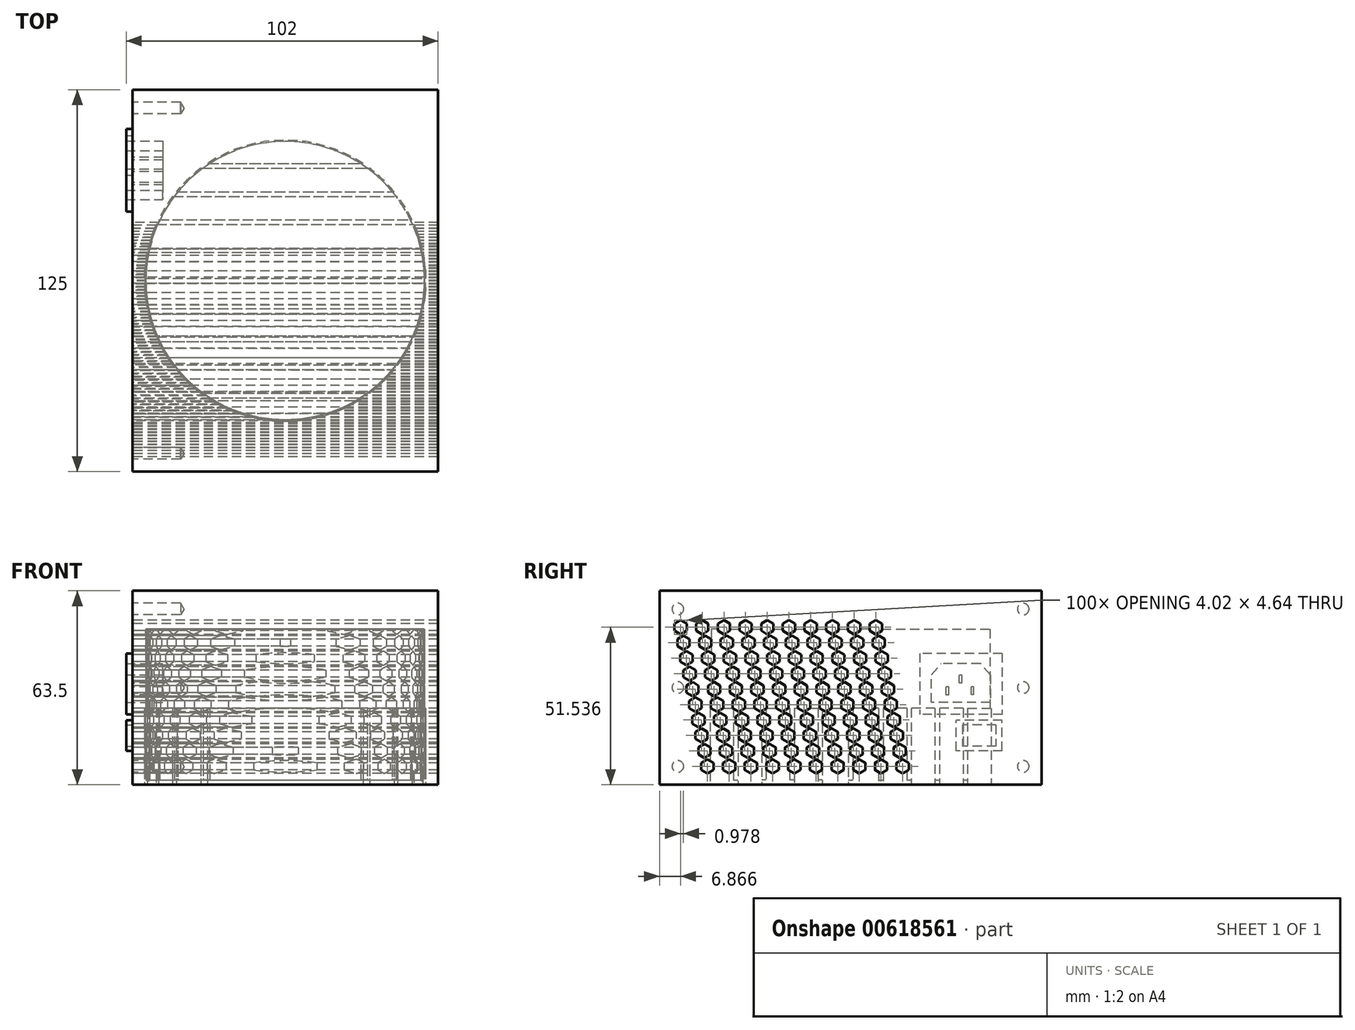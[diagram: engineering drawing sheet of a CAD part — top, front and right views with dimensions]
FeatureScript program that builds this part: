
annotation { "Feature Type Name" : "Feature", "Feature Type Description" : "" }
export const myFeature = defineFeature(function(context is Context, id is Id, definition is map)
    precondition{}
    {
        {
            var Q0;
            Q0=qCreatedBy(makeId("Top.planeOp"),FACE);
            var sketch = newSketch(context, id + "F0", { "sketchPlane" : qUnion([Q0])});
            skLineSegment(sketch, "E0.bottom", {"start": v(50, 62.5) * mm, "end": v(-50, 62.5) * mm});
            skLineSegment(sketch, "E0.top", {"start": v(50, -62.5) * mm, "end": v(-50, -62.5) * mm});
            skLineSegment(sketch, "E0.left", {"start": v(50, 62.5) * mm, "end": v(50, -62.5) * mm});
            skLineSegment(sketch, "E0.right", {"start": v(-50, 62.5) * mm, "end": v(-50, -62.5) * mm});
            skPoint(sketch, "E0.middle", {"position": v(0, 0) * mm});
            skSolve(sketch);
        }
        {
            var Q0;
            Q0=qSketchRegion(id+"F0",true);
            extrude(context, id + "F1", {"entities" : qUnion([Q0]), "depth" : 63.5 * mm, "offsetDistance" : 25 * mm});
        }
        {
            var Q0;
            Q0=makeQuery(id+"F1.opExtrude","SWEPT_FACE",FACE,{"disambiguationData":[OSD([sQuery(id+"F0.wireOp",EDGE,"E0.right")])]});
            var sketch = newSketch(context, id + "F2", { "sketchPlane" : qUnion([Q0])});
            skPoint(sketch, "E1", {"position": v(-56.5, 6) * mm});
            skPoint(sketch, "E2", {"position": v(-56.5, 57.5) * mm});
            skPoint(sketch, "E3", {"position": v(-56.5, 31.8) * mm});
            skPoint(sketch, "E4", {"position": v(56.5, 6) * mm});
            skPoint(sketch, "E5", {"position": v(56.5, 31.8) * mm});
            skPoint(sketch, "E6", {"position": v(56.5, 57.5) * mm});
            skLineSegment(sketch, "E7.bottom", {"start": v(-49.6, 42.98) * mm, "end": v(-22.6, 42.98) * mm});
            skLineSegment(sketch, "E7.top", {"start": v(-49.6, 22.98) * mm, "end": v(-22.6, 22.98) * mm});
            skLineSegment(sketch, "E7.left", {"start": v(-49.6, 42.98) * mm, "end": v(-49.6, 22.98) * mm});
            skLineSegment(sketch, "E7.right", {"start": v(-22.6, 42.98) * mm, "end": v(-22.6, 22.98) * mm});
            skLineSegment(sketch, "E8.bottom", {"start": v(-49.6, 11.07) * mm, "end": v(-34.6, 11.07) * mm});
            skLineSegment(sketch, "E8.top", {"start": v(-49.6, 21.07) * mm, "end": v(-34.6, 21.07) * mm});
            skLineSegment(sketch, "E8.left", {"start": v(-49.6, 11.07) * mm, "end": v(-49.6, 21.07) * mm});
            skLineSegment(sketch, "E8.right", {"start": v(-34.6, 11.07) * mm, "end": v(-34.6, 21.07) * mm});
            skLineSegment(sketch, "E9", {"start": v(-56.5, 6) * mm, "end": v(56.5, 6) * mm});
            skCircle(sketch, "E10.cCircle", {"center": v(-17.07, 6) * mm, "radius": 2 * mm, "construction": true});
            skLineSegment(sketch, "E10.0", {"start": v(-15.06, 7.16) * mm, "end": v(-15.06, 4.84) * mm});
            skLineSegment(sketch, "E10.1", {"start": v(-15.06, 4.84) * mm, "end": v(-17.07, 3.68) * mm});
            skLineSegment(sketch, "E10.2", {"start": v(-17.07, 3.68) * mm, "end": v(-19.08, 4.84) * mm});
            skLineSegment(sketch, "E10.3", {"start": v(-19.08, 4.84) * mm, "end": v(-19.08, 7.16) * mm});
            skLineSegment(sketch, "E10.4", {"start": v(-19.08, 7.16) * mm, "end": v(-17.07, 8.32) * mm});
            skLineSegment(sketch, "E10.5", {"start": v(-17.07, 8.32) * mm, "end": v(-15.06, 7.16) * mm});
            skPoint(sketch, "E10.0.midPoint", {"position": v(-15.06, 6) * mm});
            skLineSegment(sketch, "E11.0.1.0", {"start": v(-18.1, 12.22) * mm, "end": v(-16.1, 13.38) * mm});
            skLineSegment(sketch, "E11.0.1.1", {"start": v(-16.1, 13.38) * mm, "end": v(-14.08, 12.22) * mm});
            skLineSegment(sketch, "E11.0.1.2", {"start": v(-14.08, 12.22) * mm, "end": v(-14.08, 9.9) * mm});
            skLineSegment(sketch, "E11.0.1.3", {"start": v(-14.08, 9.9) * mm, "end": v(-16.1, 8.74) * mm});
            skLineSegment(sketch, "E11.0.1.4", {"start": v(-16.1, 8.74) * mm, "end": v(-18.1, 9.9) * mm});
            skLineSegment(sketch, "E11.0.1.5", {"start": v(-18.1, 9.9) * mm, "end": v(-18.1, 12.22) * mm});
            skLineSegment(sketch, "E11.0.2.0", {"start": v(-17.12, 17.28) * mm, "end": v(-15.11, 18.44) * mm});
            skLineSegment(sketch, "E11.0.2.1", {"start": v(-15.11, 18.44) * mm, "end": v(-13.1, 17.28) * mm});
            skLineSegment(sketch, "E11.0.2.2", {"start": v(-13.1, 17.28) * mm, "end": v(-13.1, 14.96) * mm});
            skLineSegment(sketch, "E11.0.2.3", {"start": v(-13.1, 14.96) * mm, "end": v(-15.11, 13.8) * mm});
            skLineSegment(sketch, "E11.0.2.4", {"start": v(-15.11, 13.8) * mm, "end": v(-17.12, 14.96) * mm});
            skLineSegment(sketch, "E11.0.2.5", {"start": v(-17.12, 14.96) * mm, "end": v(-17.12, 17.28) * mm});
            skLineSegment(sketch, "E11.0.3.0", {"start": v(-16.14, 22.34) * mm, "end": v(-14.14, 23.5) * mm});
            skLineSegment(sketch, "E11.0.3.1", {"start": v(-14.14, 23.5) * mm, "end": v(-12.13, 22.34) * mm});
            skLineSegment(sketch, "E11.0.3.2", {"start": v(-12.13, 22.34) * mm, "end": v(-12.13, 20.02) * mm});
            skLineSegment(sketch, "E11.0.3.3", {"start": v(-12.13, 20.02) * mm, "end": v(-14.14, 18.86) * mm});
            skLineSegment(sketch, "E11.0.3.4", {"start": v(-14.14, 18.86) * mm, "end": v(-16.14, 20.02) * mm});
            skLineSegment(sketch, "E11.0.3.5", {"start": v(-16.14, 20.02) * mm, "end": v(-16.14, 22.34) * mm});
            skLineSegment(sketch, "E11.0.4.0", {"start": v(-15.17, 27.4) * mm, "end": v(-13.16, 28.56) * mm});
            skLineSegment(sketch, "E11.0.4.1", {"start": v(-13.16, 28.56) * mm, "end": v(-11.15, 27.4) * mm});
            skLineSegment(sketch, "E11.0.4.2", {"start": v(-11.15, 27.4) * mm, "end": v(-11.15, 25.08) * mm});
            skLineSegment(sketch, "E11.0.4.3", {"start": v(-11.15, 25.08) * mm, "end": v(-13.16, 23.92) * mm});
            skLineSegment(sketch, "E11.0.4.4", {"start": v(-13.16, 23.92) * mm, "end": v(-15.17, 25.08) * mm});
            skLineSegment(sketch, "E11.0.4.5", {"start": v(-15.17, 25.08) * mm, "end": v(-15.17, 27.4) * mm});
            skLineSegment(sketch, "E11.0.5.0", {"start": v(-14.19, 32.46) * mm, "end": v(-12.18, 33.62) * mm});
            skLineSegment(sketch, "E11.0.5.1", {"start": v(-12.18, 33.62) * mm, "end": v(-10.17, 32.46) * mm});
            skLineSegment(sketch, "E11.0.5.2", {"start": v(-10.17, 32.46) * mm, "end": v(-10.17, 30.14) * mm});
            skLineSegment(sketch, "E11.0.5.3", {"start": v(-10.17, 30.14) * mm, "end": v(-12.18, 28.98) * mm});
            skLineSegment(sketch, "E11.0.5.4", {"start": v(-12.18, 28.98) * mm, "end": v(-14.19, 30.14) * mm});
            skLineSegment(sketch, "E11.0.5.5", {"start": v(-14.19, 30.14) * mm, "end": v(-14.19, 32.46) * mm});
            skLineSegment(sketch, "E11.0.6.0", {"start": v(-13.2, 37.52) * mm, "end": v(-11.2, 38.68) * mm});
            skLineSegment(sketch, "E11.0.6.1", {"start": v(-11.2, 38.68) * mm, "end": v(-9.2, 37.52) * mm});
            skLineSegment(sketch, "E11.0.6.2", {"start": v(-9.2, 37.52) * mm, "end": v(-9.2, 35.2) * mm});
            skLineSegment(sketch, "E11.0.6.3", {"start": v(-9.2, 35.2) * mm, "end": v(-11.2, 34.04) * mm});
            skLineSegment(sketch, "E11.0.6.4", {"start": v(-11.2, 34.04) * mm, "end": v(-13.2, 35.2) * mm});
            skLineSegment(sketch, "E11.0.6.5", {"start": v(-13.2, 35.2) * mm, "end": v(-13.2, 37.52) * mm});
            skLineSegment(sketch, "E11.0.7.0", {"start": v(-12.23, 42.58) * mm, "end": v(-10.22, 43.74) * mm});
            skLineSegment(sketch, "E11.0.7.1", {"start": v(-10.22, 43.74) * mm, "end": v(-8.21, 42.58) * mm});
            skLineSegment(sketch, "E11.0.7.2", {"start": v(-8.21, 42.58) * mm, "end": v(-8.21, 40.26) * mm});
            skLineSegment(sketch, "E11.0.7.3", {"start": v(-8.21, 40.26) * mm, "end": v(-10.22, 39.1) * mm});
            skLineSegment(sketch, "E11.0.7.4", {"start": v(-10.22, 39.1) * mm, "end": v(-12.23, 40.26) * mm});
            skLineSegment(sketch, "E11.0.7.5", {"start": v(-12.23, 40.26) * mm, "end": v(-12.23, 42.58) * mm});
            skLineSegment(sketch, "E11.0.8.0", {"start": v(-11.25, 47.64) * mm, "end": v(-9.24, 48.8) * mm});
            skLineSegment(sketch, "E11.0.8.1", {"start": v(-9.24, 48.8) * mm, "end": v(-7.24, 47.64) * mm});
            skLineSegment(sketch, "E11.0.8.2", {"start": v(-7.24, 47.64) * mm, "end": v(-7.24, 45.32) * mm});
            skLineSegment(sketch, "E11.0.8.3", {"start": v(-7.24, 45.32) * mm, "end": v(-9.24, 44.16) * mm});
            skLineSegment(sketch, "E11.0.8.4", {"start": v(-9.24, 44.16) * mm, "end": v(-11.25, 45.32) * mm});
            skLineSegment(sketch, "E11.0.8.5", {"start": v(-11.25, 45.32) * mm, "end": v(-11.25, 47.64) * mm});
            skLineSegment(sketch, "E11.0.9.0", {"start": v(-10.27, 52.7) * mm, "end": v(-8.27, 53.86) * mm});
            skLineSegment(sketch, "E11.0.9.1", {"start": v(-8.27, 53.86) * mm, "end": v(-6.26, 52.7) * mm});
            skLineSegment(sketch, "E11.0.9.2", {"start": v(-6.26, 52.7) * mm, "end": v(-6.26, 50.38) * mm});
            skLineSegment(sketch, "E11.0.9.3", {"start": v(-6.26, 50.38) * mm, "end": v(-8.27, 49.22) * mm});
            skLineSegment(sketch, "E11.0.9.4", {"start": v(-8.27, 49.22) * mm, "end": v(-10.27, 50.38) * mm});
            skLineSegment(sketch, "E11.0.9.5", {"start": v(-10.27, 50.38) * mm, "end": v(-10.27, 52.7) * mm});
            skLineSegment(sketch, "E11.1.0.0", {"start": v(-11.98, 7.16) * mm, "end": v(-9.97, 8.32) * mm});
            skLineSegment(sketch, "E11.1.0.1", {"start": v(-9.97, 8.32) * mm, "end": v(-7.96, 7.16) * mm});
            skLineSegment(sketch, "E11.1.0.2", {"start": v(-7.96, 7.16) * mm, "end": v(-7.96, 4.84) * mm});
            skLineSegment(sketch, "E11.1.0.3", {"start": v(-7.96, 4.84) * mm, "end": v(-9.97, 3.68) * mm});
            skLineSegment(sketch, "E11.1.0.4", {"start": v(-9.97, 3.68) * mm, "end": v(-11.98, 4.84) * mm});
            skLineSegment(sketch, "E11.1.0.5", {"start": v(-11.98, 4.84) * mm, "end": v(-11.98, 7.16) * mm});
            skLineSegment(sketch, "E11.1.1.0", {"start": v(-11, 12.22) * mm, "end": v(-9, 13.38) * mm});
            skLineSegment(sketch, "E11.1.1.1", {"start": v(-9, 13.38) * mm, "end": v(-6.98, 12.22) * mm});
            skLineSegment(sketch, "E11.1.1.2", {"start": v(-6.98, 12.22) * mm, "end": v(-6.98, 9.9) * mm});
            skLineSegment(sketch, "E11.1.1.3", {"start": v(-6.98, 9.9) * mm, "end": v(-9, 8.74) * mm});
            skLineSegment(sketch, "E11.1.1.4", {"start": v(-9, 8.74) * mm, "end": v(-11, 9.9) * mm});
            skLineSegment(sketch, "E11.1.1.5", {"start": v(-11, 9.9) * mm, "end": v(-11, 12.22) * mm});
            skLineSegment(sketch, "E11.1.2.0", {"start": v(-10.02, 17.28) * mm, "end": v(-8.01, 18.44) * mm});
            skLineSegment(sketch, "E11.1.2.1", {"start": v(-8.01, 18.44) * mm, "end": v(-6, 17.28) * mm});
            skLineSegment(sketch, "E11.1.2.2", {"start": v(-6, 17.28) * mm, "end": v(-6, 14.96) * mm});
            skLineSegment(sketch, "E11.1.2.3", {"start": v(-6, 14.96) * mm, "end": v(-8.01, 13.8) * mm});
            skLineSegment(sketch, "E11.1.2.4", {"start": v(-8.01, 13.8) * mm, "end": v(-10.02, 14.96) * mm});
            skLineSegment(sketch, "E11.1.2.5", {"start": v(-10.02, 14.96) * mm, "end": v(-10.02, 17.28) * mm});
            skLineSegment(sketch, "E11.1.3.0", {"start": v(-9.04, 22.34) * mm, "end": v(-7.04, 23.5) * mm});
            skLineSegment(sketch, "E11.1.3.1", {"start": v(-7.04, 23.5) * mm, "end": v(-5.03, 22.34) * mm});
            skLineSegment(sketch, "E11.1.3.2", {"start": v(-5.03, 22.34) * mm, "end": v(-5.03, 20.02) * mm});
            skLineSegment(sketch, "E11.1.3.3", {"start": v(-5.03, 20.02) * mm, "end": v(-7.04, 18.86) * mm});
            skLineSegment(sketch, "E11.1.3.4", {"start": v(-7.04, 18.86) * mm, "end": v(-9.04, 20.02) * mm});
            skLineSegment(sketch, "E11.1.3.5", {"start": v(-9.04, 20.02) * mm, "end": v(-9.04, 22.34) * mm});
            skLineSegment(sketch, "E11.1.4.0", {"start": v(-8.07, 27.4) * mm, "end": v(-6.06, 28.56) * mm});
            skLineSegment(sketch, "E11.1.4.1", {"start": v(-6.06, 28.56) * mm, "end": v(-4.05, 27.4) * mm});
            skLineSegment(sketch, "E11.1.4.2", {"start": v(-4.05, 27.4) * mm, "end": v(-4.05, 25.08) * mm});
            skLineSegment(sketch, "E11.1.4.3", {"start": v(-4.05, 25.08) * mm, "end": v(-6.06, 23.92) * mm});
            skLineSegment(sketch, "E11.1.4.4", {"start": v(-6.06, 23.92) * mm, "end": v(-8.07, 25.08) * mm});
            skLineSegment(sketch, "E11.1.4.5", {"start": v(-8.07, 25.08) * mm, "end": v(-8.07, 27.4) * mm});
            skLineSegment(sketch, "E11.1.5.0", {"start": v(-7.09, 32.46) * mm, "end": v(-5.08, 33.62) * mm});
            skLineSegment(sketch, "E11.1.5.1", {"start": v(-5.08, 33.62) * mm, "end": v(-3.07, 32.46) * mm});
            skLineSegment(sketch, "E11.1.5.2", {"start": v(-3.07, 32.46) * mm, "end": v(-3.07, 30.14) * mm});
            skLineSegment(sketch, "E11.1.5.3", {"start": v(-3.07, 30.14) * mm, "end": v(-5.08, 28.98) * mm});
            skLineSegment(sketch, "E11.1.5.4", {"start": v(-5.08, 28.98) * mm, "end": v(-7.09, 30.14) * mm});
            skLineSegment(sketch, "E11.1.5.5", {"start": v(-7.09, 30.14) * mm, "end": v(-7.09, 32.46) * mm});
            skLineSegment(sketch, "E11.1.6.0", {"start": v(-6.1, 37.52) * mm, "end": v(-4.1, 38.68) * mm});
            skLineSegment(sketch, "E11.1.6.1", {"start": v(-4.1, 38.68) * mm, "end": v(-2.1, 37.52) * mm});
            skLineSegment(sketch, "E11.1.6.2", {"start": v(-2.1, 37.52) * mm, "end": v(-2.1, 35.2) * mm});
            skLineSegment(sketch, "E11.1.6.3", {"start": v(-2.1, 35.2) * mm, "end": v(-4.1, 34.04) * mm});
            skLineSegment(sketch, "E11.1.6.4", {"start": v(-4.1, 34.04) * mm, "end": v(-6.1, 35.2) * mm});
            skLineSegment(sketch, "E11.1.6.5", {"start": v(-6.1, 35.2) * mm, "end": v(-6.1, 37.52) * mm});
            skLineSegment(sketch, "E11.1.7.0", {"start": v(-5.13, 42.58) * mm, "end": v(-3.12, 43.74) * mm});
            skLineSegment(sketch, "E11.1.7.1", {"start": v(-3.12, 43.74) * mm, "end": v(-1.11, 42.58) * mm});
            skLineSegment(sketch, "E11.1.7.2", {"start": v(-1.11, 42.58) * mm, "end": v(-1.11, 40.26) * mm});
            skLineSegment(sketch, "E11.1.7.3", {"start": v(-1.11, 40.26) * mm, "end": v(-3.12, 39.1) * mm});
            skLineSegment(sketch, "E11.1.7.4", {"start": v(-3.12, 39.1) * mm, "end": v(-5.13, 40.26) * mm});
            skLineSegment(sketch, "E11.1.7.5", {"start": v(-5.13, 40.26) * mm, "end": v(-5.13, 42.58) * mm});
            skLineSegment(sketch, "E11.1.8.0", {"start": v(-4.15, 47.64) * mm, "end": v(-2.14, 48.8) * mm});
            skLineSegment(sketch, "E11.1.8.1", {"start": v(-2.14, 48.8) * mm, "end": v(-0.14, 47.64) * mm});
            skLineSegment(sketch, "E11.1.8.2", {"start": v(-0.14, 47.64) * mm, "end": v(-0.14, 45.32) * mm});
            skLineSegment(sketch, "E11.1.8.3", {"start": v(-0.14, 45.32) * mm, "end": v(-2.14, 44.16) * mm});
            skLineSegment(sketch, "E11.1.8.4", {"start": v(-2.14, 44.16) * mm, "end": v(-4.15, 45.32) * mm});
            skLineSegment(sketch, "E11.1.8.5", {"start": v(-4.15, 45.32) * mm, "end": v(-4.15, 47.64) * mm});
            skLineSegment(sketch, "E11.1.9.0", {"start": v(-3.17, 52.7) * mm, "end": v(-1.17, 53.86) * mm});
            skLineSegment(sketch, "E11.1.9.1", {"start": v(-1.17, 53.86) * mm, "end": v(0.84, 52.7) * mm});
            skLineSegment(sketch, "E11.1.9.2", {"start": v(0.84, 52.7) * mm, "end": v(0.84, 50.38) * mm});
            skLineSegment(sketch, "E11.1.9.3", {"start": v(0.84, 50.38) * mm, "end": v(-1.17, 49.22) * mm});
            skLineSegment(sketch, "E11.1.9.4", {"start": v(-1.17, 49.22) * mm, "end": v(-3.17, 50.38) * mm});
            skLineSegment(sketch, "E11.1.9.5", {"start": v(-3.17, 50.38) * mm, "end": v(-3.17, 52.7) * mm});
            skLineSegment(sketch, "E11.2.0.0", {"start": v(-4.88, 7.16) * mm, "end": v(-2.87, 8.32) * mm});
            skLineSegment(sketch, "E11.2.0.1", {"start": v(-2.87, 8.32) * mm, "end": v(-0.86, 7.16) * mm});
            skLineSegment(sketch, "E11.2.0.2", {"start": v(-0.86, 7.16) * mm, "end": v(-0.86, 4.84) * mm});
            skLineSegment(sketch, "E11.2.0.3", {"start": v(-0.86, 4.84) * mm, "end": v(-2.87, 3.68) * mm});
            skLineSegment(sketch, "E11.2.0.4", {"start": v(-2.87, 3.68) * mm, "end": v(-4.88, 4.84) * mm});
            skLineSegment(sketch, "E11.2.0.5", {"start": v(-4.88, 4.84) * mm, "end": v(-4.88, 7.16) * mm});
            skLineSegment(sketch, "E11.2.1.0", {"start": v(-3.9, 12.22) * mm, "end": v(-1.9, 13.38) * mm});
            skLineSegment(sketch, "E11.2.1.1", {"start": v(-1.9, 13.38) * mm, "end": v(0.12, 12.22) * mm});
            skLineSegment(sketch, "E11.2.1.2", {"start": v(0.12, 12.22) * mm, "end": v(0.12, 9.9) * mm});
            skLineSegment(sketch, "E11.2.1.3", {"start": v(0.12, 9.9) * mm, "end": v(-1.9, 8.74) * mm});
            skLineSegment(sketch, "E11.2.1.4", {"start": v(-1.9, 8.74) * mm, "end": v(-3.9, 9.9) * mm});
            skLineSegment(sketch, "E11.2.1.5", {"start": v(-3.9, 9.9) * mm, "end": v(-3.9, 12.22) * mm});
            skLineSegment(sketch, "E11.2.2.0", {"start": v(-2.92, 17.28) * mm, "end": v(-0.91, 18.44) * mm});
            skLineSegment(sketch, "E11.2.2.1", {"start": v(-0.91, 18.44) * mm, "end": v(1.1, 17.28) * mm});
            skLineSegment(sketch, "E11.2.2.2", {"start": v(1.1, 17.28) * mm, "end": v(1.1, 14.96) * mm});
            skLineSegment(sketch, "E11.2.2.3", {"start": v(1.1, 14.96) * mm, "end": v(-0.91, 13.8) * mm});
            skLineSegment(sketch, "E11.2.2.4", {"start": v(-0.91, 13.8) * mm, "end": v(-2.92, 14.96) * mm});
            skLineSegment(sketch, "E11.2.2.5", {"start": v(-2.92, 14.96) * mm, "end": v(-2.92, 17.28) * mm});
            skLineSegment(sketch, "E11.2.3.0", {"start": v(-1.94, 22.34) * mm, "end": v(0.06, 23.5) * mm});
            skLineSegment(sketch, "E11.2.3.1", {"start": v(0.06, 23.5) * mm, "end": v(2.07, 22.34) * mm});
            skLineSegment(sketch, "E11.2.3.2", {"start": v(2.07, 22.34) * mm, "end": v(2.07, 20.02) * mm});
            skLineSegment(sketch, "E11.2.3.3", {"start": v(2.07, 20.02) * mm, "end": v(0.06, 18.86) * mm});
            skLineSegment(sketch, "E11.2.3.4", {"start": v(0.06, 18.86) * mm, "end": v(-1.94, 20.02) * mm});
            skLineSegment(sketch, "E11.2.3.5", {"start": v(-1.94, 20.02) * mm, "end": v(-1.94, 22.34) * mm});
            skLineSegment(sketch, "E11.2.4.0", {"start": v(-0.97, 27.4) * mm, "end": v(1.04, 28.56) * mm});
            skLineSegment(sketch, "E11.2.4.1", {"start": v(1.04, 28.56) * mm, "end": v(3.05, 27.4) * mm});
            skLineSegment(sketch, "E11.2.4.2", {"start": v(3.05, 27.4) * mm, "end": v(3.05, 25.08) * mm});
            skLineSegment(sketch, "E11.2.4.3", {"start": v(3.05, 25.08) * mm, "end": v(1.04, 23.92) * mm});
            skLineSegment(sketch, "E11.2.4.4", {"start": v(1.04, 23.92) * mm, "end": v(-0.97, 25.08) * mm});
            skLineSegment(sketch, "E11.2.4.5", {"start": v(-0.97, 25.08) * mm, "end": v(-0.97, 27.4) * mm});
            skLineSegment(sketch, "E11.2.5.0", {"start": v(0.01, 32.46) * mm, "end": v(2.02, 33.62) * mm});
            skLineSegment(sketch, "E11.2.5.1", {"start": v(2.02, 33.62) * mm, "end": v(4.03, 32.46) * mm});
            skLineSegment(sketch, "E11.2.5.2", {"start": v(4.03, 32.46) * mm, "end": v(4.03, 30.14) * mm});
            skLineSegment(sketch, "E11.2.5.3", {"start": v(4.03, 30.14) * mm, "end": v(2.02, 28.98) * mm});
            skLineSegment(sketch, "E11.2.5.4", {"start": v(2.02, 28.98) * mm, "end": v(0.01, 30.14) * mm});
            skLineSegment(sketch, "E11.2.5.5", {"start": v(0.01, 30.14) * mm, "end": v(0.01, 32.46) * mm});
            skLineSegment(sketch, "E11.2.6.0", {"start": v(1, 37.52) * mm, "end": v(3, 38.68) * mm});
            skLineSegment(sketch, "E11.2.6.1", {"start": v(3, 38.68) * mm, "end": v(5, 37.52) * mm});
            skLineSegment(sketch, "E11.2.6.2", {"start": v(5, 37.52) * mm, "end": v(5, 35.2) * mm});
            skLineSegment(sketch, "E11.2.6.3", {"start": v(5, 35.2) * mm, "end": v(3, 34.04) * mm});
            skLineSegment(sketch, "E11.2.6.4", {"start": v(3, 34.04) * mm, "end": v(1, 35.2) * mm});
            skLineSegment(sketch, "E11.2.6.5", {"start": v(1, 35.2) * mm, "end": v(1, 37.52) * mm});
            skLineSegment(sketch, "E11.2.7.0", {"start": v(1.97, 42.58) * mm, "end": v(3.98, 43.74) * mm});
            skLineSegment(sketch, "E11.2.7.1", {"start": v(3.98, 43.74) * mm, "end": v(5.99, 42.58) * mm});
            skLineSegment(sketch, "E11.2.7.2", {"start": v(5.99, 42.58) * mm, "end": v(5.99, 40.26) * mm});
            skLineSegment(sketch, "E11.2.7.3", {"start": v(5.99, 40.26) * mm, "end": v(3.98, 39.1) * mm});
            skLineSegment(sketch, "E11.2.7.4", {"start": v(3.98, 39.1) * mm, "end": v(1.97, 40.26) * mm});
            skLineSegment(sketch, "E11.2.7.5", {"start": v(1.97, 40.26) * mm, "end": v(1.97, 42.58) * mm});
            skLineSegment(sketch, "E11.2.8.0", {"start": v(2.95, 47.64) * mm, "end": v(4.96, 48.8) * mm});
            skLineSegment(sketch, "E11.2.8.1", {"start": v(4.96, 48.8) * mm, "end": v(6.96, 47.64) * mm});
            skLineSegment(sketch, "E11.2.8.2", {"start": v(6.96, 47.64) * mm, "end": v(6.96, 45.32) * mm});
            skLineSegment(sketch, "E11.2.8.3", {"start": v(6.96, 45.32) * mm, "end": v(4.96, 44.16) * mm});
            skLineSegment(sketch, "E11.2.8.4", {"start": v(4.96, 44.16) * mm, "end": v(2.95, 45.32) * mm});
            skLineSegment(sketch, "E11.2.8.5", {"start": v(2.95, 45.32) * mm, "end": v(2.95, 47.64) * mm});
            skLineSegment(sketch, "E11.2.9.0", {"start": v(3.93, 52.7) * mm, "end": v(5.93, 53.86) * mm});
            skLineSegment(sketch, "E11.2.9.1", {"start": v(5.93, 53.86) * mm, "end": v(7.94, 52.7) * mm});
            skLineSegment(sketch, "E11.2.9.2", {"start": v(7.94, 52.7) * mm, "end": v(7.94, 50.38) * mm});
            skLineSegment(sketch, "E11.2.9.3", {"start": v(7.94, 50.38) * mm, "end": v(5.93, 49.22) * mm});
            skLineSegment(sketch, "E11.2.9.4", {"start": v(5.93, 49.22) * mm, "end": v(3.93, 50.38) * mm});
            skLineSegment(sketch, "E11.2.9.5", {"start": v(3.93, 50.38) * mm, "end": v(3.93, 52.7) * mm});
            skLineSegment(sketch, "E11.3.0.0", {"start": v(2.22, 7.16) * mm, "end": v(4.23, 8.32) * mm});
            skLineSegment(sketch, "E11.3.0.1", {"start": v(4.23, 8.32) * mm, "end": v(6.24, 7.16) * mm});
            skLineSegment(sketch, "E11.3.0.2", {"start": v(6.24, 7.16) * mm, "end": v(6.24, 4.84) * mm});
            skLineSegment(sketch, "E11.3.0.3", {"start": v(6.24, 4.84) * mm, "end": v(4.23, 3.68) * mm});
            skLineSegment(sketch, "E11.3.0.4", {"start": v(4.23, 3.68) * mm, "end": v(2.22, 4.84) * mm});
            skLineSegment(sketch, "E11.3.0.5", {"start": v(2.22, 4.84) * mm, "end": v(2.22, 7.16) * mm});
            skLineSegment(sketch, "E11.3.1.0", {"start": v(3.2, 12.22) * mm, "end": v(5.2, 13.38) * mm});
            skLineSegment(sketch, "E11.3.1.1", {"start": v(5.2, 13.38) * mm, "end": v(7.22, 12.22) * mm});
            skLineSegment(sketch, "E11.3.1.2", {"start": v(7.22, 12.22) * mm, "end": v(7.22, 9.9) * mm});
            skLineSegment(sketch, "E11.3.1.3", {"start": v(7.22, 9.9) * mm, "end": v(5.2, 8.74) * mm});
            skLineSegment(sketch, "E11.3.1.4", {"start": v(5.2, 8.74) * mm, "end": v(3.2, 9.9) * mm});
            skLineSegment(sketch, "E11.3.1.5", {"start": v(3.2, 9.9) * mm, "end": v(3.2, 12.22) * mm});
            skLineSegment(sketch, "E11.3.2.0", {"start": v(4.18, 17.28) * mm, "end": v(6.19, 18.44) * mm});
            skLineSegment(sketch, "E11.3.2.1", {"start": v(6.19, 18.44) * mm, "end": v(8.2, 17.28) * mm});
            skLineSegment(sketch, "E11.3.2.2", {"start": v(8.2, 17.28) * mm, "end": v(8.2, 14.96) * mm});
            skLineSegment(sketch, "E11.3.2.3", {"start": v(8.2, 14.96) * mm, "end": v(6.19, 13.8) * mm});
            skLineSegment(sketch, "E11.3.2.4", {"start": v(6.19, 13.8) * mm, "end": v(4.18, 14.96) * mm});
            skLineSegment(sketch, "E11.3.2.5", {"start": v(4.18, 14.96) * mm, "end": v(4.18, 17.28) * mm});
            skLineSegment(sketch, "E11.3.3.0", {"start": v(5.16, 22.34) * mm, "end": v(7.16, 23.5) * mm});
            skLineSegment(sketch, "E11.3.3.1", {"start": v(7.16, 23.5) * mm, "end": v(9.17, 22.34) * mm});
            skLineSegment(sketch, "E11.3.3.2", {"start": v(9.17, 22.34) * mm, "end": v(9.17, 20.02) * mm});
            skLineSegment(sketch, "E11.3.3.3", {"start": v(9.17, 20.02) * mm, "end": v(7.16, 18.86) * mm});
            skLineSegment(sketch, "E11.3.3.4", {"start": v(7.16, 18.86) * mm, "end": v(5.16, 20.02) * mm});
            skLineSegment(sketch, "E11.3.3.5", {"start": v(5.16, 20.02) * mm, "end": v(5.16, 22.34) * mm});
            skLineSegment(sketch, "E11.3.4.0", {"start": v(6.13, 27.4) * mm, "end": v(8.14, 28.56) * mm});
            skLineSegment(sketch, "E11.3.4.1", {"start": v(8.14, 28.56) * mm, "end": v(10.15, 27.4) * mm});
            skLineSegment(sketch, "E11.3.4.2", {"start": v(10.15, 27.4) * mm, "end": v(10.15, 25.08) * mm});
            skLineSegment(sketch, "E11.3.4.3", {"start": v(10.15, 25.08) * mm, "end": v(8.14, 23.92) * mm});
            skLineSegment(sketch, "E11.3.4.4", {"start": v(8.14, 23.92) * mm, "end": v(6.13, 25.08) * mm});
            skLineSegment(sketch, "E11.3.4.5", {"start": v(6.13, 25.08) * mm, "end": v(6.13, 27.4) * mm});
            skLineSegment(sketch, "E11.3.5.0", {"start": v(7.11, 32.46) * mm, "end": v(9.12, 33.62) * mm});
            skLineSegment(sketch, "E11.3.5.1", {"start": v(9.12, 33.62) * mm, "end": v(11.13, 32.46) * mm});
            skLineSegment(sketch, "E11.3.5.2", {"start": v(11.13, 32.46) * mm, "end": v(11.13, 30.14) * mm});
            skLineSegment(sketch, "E11.3.5.3", {"start": v(11.13, 30.14) * mm, "end": v(9.12, 28.98) * mm});
            skLineSegment(sketch, "E11.3.5.4", {"start": v(9.12, 28.98) * mm, "end": v(7.11, 30.14) * mm});
            skLineSegment(sketch, "E11.3.5.5", {"start": v(7.11, 30.14) * mm, "end": v(7.11, 32.46) * mm});
            skLineSegment(sketch, "E11.3.6.0", {"start": v(8.1, 37.52) * mm, "end": v(10.1, 38.68) * mm});
            skLineSegment(sketch, "E11.3.6.1", {"start": v(10.1, 38.68) * mm, "end": v(12.1, 37.52) * mm});
            skLineSegment(sketch, "E11.3.6.2", {"start": v(12.1, 37.52) * mm, "end": v(12.1, 35.2) * mm});
            skLineSegment(sketch, "E11.3.6.3", {"start": v(12.1, 35.2) * mm, "end": v(10.1, 34.04) * mm});
            skLineSegment(sketch, "E11.3.6.4", {"start": v(10.1, 34.04) * mm, "end": v(8.1, 35.2) * mm});
            skLineSegment(sketch, "E11.3.6.5", {"start": v(8.1, 35.2) * mm, "end": v(8.1, 37.52) * mm});
            skLineSegment(sketch, "E11.3.7.0", {"start": v(9.07, 42.58) * mm, "end": v(11.08, 43.74) * mm});
            skLineSegment(sketch, "E11.3.7.1", {"start": v(11.08, 43.74) * mm, "end": v(13.09, 42.58) * mm});
            skLineSegment(sketch, "E11.3.7.2", {"start": v(13.09, 42.58) * mm, "end": v(13.09, 40.26) * mm});
            skLineSegment(sketch, "E11.3.7.3", {"start": v(13.09, 40.26) * mm, "end": v(11.08, 39.1) * mm});
            skLineSegment(sketch, "E11.3.7.4", {"start": v(11.08, 39.1) * mm, "end": v(9.07, 40.26) * mm});
            skLineSegment(sketch, "E11.3.7.5", {"start": v(9.07, 40.26) * mm, "end": v(9.07, 42.58) * mm});
            skLineSegment(sketch, "E11.3.8.0", {"start": v(10.05, 47.64) * mm, "end": v(12.06, 48.8) * mm});
            skLineSegment(sketch, "E11.3.8.1", {"start": v(12.06, 48.8) * mm, "end": v(14.06, 47.64) * mm});
            skLineSegment(sketch, "E11.3.8.2", {"start": v(14.06, 47.64) * mm, "end": v(14.06, 45.32) * mm});
            skLineSegment(sketch, "E11.3.8.3", {"start": v(14.06, 45.32) * mm, "end": v(12.06, 44.16) * mm});
            skLineSegment(sketch, "E11.3.8.4", {"start": v(12.06, 44.16) * mm, "end": v(10.05, 45.32) * mm});
            skLineSegment(sketch, "E11.3.8.5", {"start": v(10.05, 45.32) * mm, "end": v(10.05, 47.64) * mm});
            skLineSegment(sketch, "E11.3.9.0", {"start": v(11.03, 52.7) * mm, "end": v(13.03, 53.86) * mm});
            skLineSegment(sketch, "E11.3.9.1", {"start": v(13.03, 53.86) * mm, "end": v(15.04, 52.7) * mm});
            skLineSegment(sketch, "E11.3.9.2", {"start": v(15.04, 52.7) * mm, "end": v(15.04, 50.38) * mm});
            skLineSegment(sketch, "E11.3.9.3", {"start": v(15.04, 50.38) * mm, "end": v(13.03, 49.22) * mm});
            skLineSegment(sketch, "E11.3.9.4", {"start": v(13.03, 49.22) * mm, "end": v(11.03, 50.38) * mm});
            skLineSegment(sketch, "E11.3.9.5", {"start": v(11.03, 50.38) * mm, "end": v(11.03, 52.7) * mm});
            skLineSegment(sketch, "E11.4.0.0", {"start": v(9.32, 7.16) * mm, "end": v(11.33, 8.32) * mm});
            skLineSegment(sketch, "E11.4.0.1", {"start": v(11.33, 8.32) * mm, "end": v(13.34, 7.16) * mm});
            skLineSegment(sketch, "E11.4.0.2", {"start": v(13.34, 7.16) * mm, "end": v(13.34, 4.84) * mm});
            skLineSegment(sketch, "E11.4.0.3", {"start": v(13.34, 4.84) * mm, "end": v(11.33, 3.68) * mm});
            skLineSegment(sketch, "E11.4.0.4", {"start": v(11.33, 3.68) * mm, "end": v(9.32, 4.84) * mm});
            skLineSegment(sketch, "E11.4.0.5", {"start": v(9.32, 4.84) * mm, "end": v(9.32, 7.16) * mm});
            skLineSegment(sketch, "E11.4.1.0", {"start": v(10.3, 12.22) * mm, "end": v(12.3, 13.38) * mm});
            skLineSegment(sketch, "E11.4.1.1", {"start": v(12.3, 13.38) * mm, "end": v(14.32, 12.22) * mm});
            skLineSegment(sketch, "E11.4.1.2", {"start": v(14.32, 12.22) * mm, "end": v(14.32, 9.9) * mm});
            skLineSegment(sketch, "E11.4.1.3", {"start": v(14.32, 9.9) * mm, "end": v(12.3, 8.74) * mm});
            skLineSegment(sketch, "E11.4.1.4", {"start": v(12.3, 8.74) * mm, "end": v(10.3, 9.9) * mm});
            skLineSegment(sketch, "E11.4.1.5", {"start": v(10.3, 9.9) * mm, "end": v(10.3, 12.22) * mm});
            skLineSegment(sketch, "E11.4.2.0", {"start": v(11.28, 17.28) * mm, "end": v(13.29, 18.44) * mm});
            skLineSegment(sketch, "E11.4.2.1", {"start": v(13.29, 18.44) * mm, "end": v(15.3, 17.28) * mm});
            skLineSegment(sketch, "E11.4.2.2", {"start": v(15.3, 17.28) * mm, "end": v(15.3, 14.96) * mm});
            skLineSegment(sketch, "E11.4.2.3", {"start": v(15.3, 14.96) * mm, "end": v(13.29, 13.8) * mm});
            skLineSegment(sketch, "E11.4.2.4", {"start": v(13.29, 13.8) * mm, "end": v(11.28, 14.96) * mm});
            skLineSegment(sketch, "E11.4.2.5", {"start": v(11.28, 14.96) * mm, "end": v(11.28, 17.28) * mm});
            skLineSegment(sketch, "E11.4.3.0", {"start": v(12.26, 22.34) * mm, "end": v(14.26, 23.5) * mm});
            skLineSegment(sketch, "E11.4.3.1", {"start": v(14.26, 23.5) * mm, "end": v(16.27, 22.34) * mm});
            skLineSegment(sketch, "E11.4.3.2", {"start": v(16.27, 22.34) * mm, "end": v(16.27, 20.02) * mm});
            skLineSegment(sketch, "E11.4.3.3", {"start": v(16.27, 20.02) * mm, "end": v(14.26, 18.86) * mm});
            skLineSegment(sketch, "E11.4.3.4", {"start": v(14.26, 18.86) * mm, "end": v(12.26, 20.02) * mm});
            skLineSegment(sketch, "E11.4.3.5", {"start": v(12.26, 20.02) * mm, "end": v(12.26, 22.34) * mm});
            skLineSegment(sketch, "E11.4.4.0", {"start": v(13.23, 27.4) * mm, "end": v(15.24, 28.56) * mm});
            skLineSegment(sketch, "E11.4.4.1", {"start": v(15.24, 28.56) * mm, "end": v(17.25, 27.4) * mm});
            skLineSegment(sketch, "E11.4.4.2", {"start": v(17.25, 27.4) * mm, "end": v(17.25, 25.08) * mm});
            skLineSegment(sketch, "E11.4.4.3", {"start": v(17.25, 25.08) * mm, "end": v(15.24, 23.92) * mm});
            skLineSegment(sketch, "E11.4.4.4", {"start": v(15.24, 23.92) * mm, "end": v(13.23, 25.08) * mm});
            skLineSegment(sketch, "E11.4.4.5", {"start": v(13.23, 25.08) * mm, "end": v(13.23, 27.4) * mm});
            skLineSegment(sketch, "E11.4.5.0", {"start": v(14.21, 32.46) * mm, "end": v(16.22, 33.62) * mm});
            skLineSegment(sketch, "E11.4.5.1", {"start": v(16.22, 33.62) * mm, "end": v(18.23, 32.46) * mm});
            skLineSegment(sketch, "E11.4.5.2", {"start": v(18.23, 32.46) * mm, "end": v(18.23, 30.14) * mm});
            skLineSegment(sketch, "E11.4.5.3", {"start": v(18.23, 30.14) * mm, "end": v(16.22, 28.98) * mm});
            skLineSegment(sketch, "E11.4.5.4", {"start": v(16.22, 28.98) * mm, "end": v(14.21, 30.14) * mm});
            skLineSegment(sketch, "E11.4.5.5", {"start": v(14.21, 30.14) * mm, "end": v(14.21, 32.46) * mm});
            skLineSegment(sketch, "E11.4.6.0", {"start": v(15.2, 37.52) * mm, "end": v(17.2, 38.68) * mm});
            skLineSegment(sketch, "E11.4.6.1", {"start": v(17.2, 38.68) * mm, "end": v(19.2, 37.52) * mm});
            skLineSegment(sketch, "E11.4.6.2", {"start": v(19.2, 37.52) * mm, "end": v(19.2, 35.2) * mm});
            skLineSegment(sketch, "E11.4.6.3", {"start": v(19.2, 35.2) * mm, "end": v(17.2, 34.04) * mm});
            skLineSegment(sketch, "E11.4.6.4", {"start": v(17.2, 34.04) * mm, "end": v(15.2, 35.2) * mm});
            skLineSegment(sketch, "E11.4.6.5", {"start": v(15.2, 35.2) * mm, "end": v(15.2, 37.52) * mm});
            skLineSegment(sketch, "E11.4.7.0", {"start": v(16.17, 42.58) * mm, "end": v(18.18, 43.74) * mm});
            skLineSegment(sketch, "E11.4.7.1", {"start": v(18.18, 43.74) * mm, "end": v(20.19, 42.58) * mm});
            skLineSegment(sketch, "E11.4.7.2", {"start": v(20.19, 42.58) * mm, "end": v(20.19, 40.26) * mm});
            skLineSegment(sketch, "E11.4.7.3", {"start": v(20.19, 40.26) * mm, "end": v(18.18, 39.1) * mm});
            skLineSegment(sketch, "E11.4.7.4", {"start": v(18.18, 39.1) * mm, "end": v(16.17, 40.26) * mm});
            skLineSegment(sketch, "E11.4.7.5", {"start": v(16.17, 40.26) * mm, "end": v(16.17, 42.58) * mm});
            skLineSegment(sketch, "E11.4.8.0", {"start": v(17.15, 47.64) * mm, "end": v(19.16, 48.8) * mm});
            skLineSegment(sketch, "E11.4.8.1", {"start": v(19.16, 48.8) * mm, "end": v(21.16, 47.64) * mm});
            skLineSegment(sketch, "E11.4.8.2", {"start": v(21.16, 47.64) * mm, "end": v(21.16, 45.32) * mm});
            skLineSegment(sketch, "E11.4.8.3", {"start": v(21.16, 45.32) * mm, "end": v(19.16, 44.16) * mm});
            skLineSegment(sketch, "E11.4.8.4", {"start": v(19.16, 44.16) * mm, "end": v(17.15, 45.32) * mm});
            skLineSegment(sketch, "E11.4.8.5", {"start": v(17.15, 45.32) * mm, "end": v(17.15, 47.64) * mm});
            skLineSegment(sketch, "E11.4.9.0", {"start": v(18.13, 52.7) * mm, "end": v(20.13, 53.86) * mm});
            skLineSegment(sketch, "E11.4.9.1", {"start": v(20.13, 53.86) * mm, "end": v(22.14, 52.7) * mm});
            skLineSegment(sketch, "E11.4.9.2", {"start": v(22.14, 52.7) * mm, "end": v(22.14, 50.38) * mm});
            skLineSegment(sketch, "E11.4.9.3", {"start": v(22.14, 50.38) * mm, "end": v(20.13, 49.22) * mm});
            skLineSegment(sketch, "E11.4.9.4", {"start": v(20.13, 49.22) * mm, "end": v(18.13, 50.38) * mm});
            skLineSegment(sketch, "E11.4.9.5", {"start": v(18.13, 50.38) * mm, "end": v(18.13, 52.7) * mm});
            skLineSegment(sketch, "E11.5.0.0", {"start": v(16.42, 7.16) * mm, "end": v(18.43, 8.32) * mm});
            skLineSegment(sketch, "E11.5.0.1", {"start": v(18.43, 8.32) * mm, "end": v(20.44, 7.16) * mm});
            skLineSegment(sketch, "E11.5.0.2", {"start": v(20.44, 7.16) * mm, "end": v(20.44, 4.84) * mm});
            skLineSegment(sketch, "E11.5.0.3", {"start": v(20.44, 4.84) * mm, "end": v(18.43, 3.68) * mm});
            skLineSegment(sketch, "E11.5.0.4", {"start": v(18.43, 3.68) * mm, "end": v(16.42, 4.84) * mm});
            skLineSegment(sketch, "E11.5.0.5", {"start": v(16.42, 4.84) * mm, "end": v(16.42, 7.16) * mm});
            skLineSegment(sketch, "E11.5.1.0", {"start": v(17.4, 12.22) * mm, "end": v(19.4, 13.38) * mm});
            skLineSegment(sketch, "E11.5.1.1", {"start": v(19.4, 13.38) * mm, "end": v(21.42, 12.22) * mm});
            skLineSegment(sketch, "E11.5.1.2", {"start": v(21.42, 12.22) * mm, "end": v(21.42, 9.9) * mm});
            skLineSegment(sketch, "E11.5.1.3", {"start": v(21.42, 9.9) * mm, "end": v(19.4, 8.74) * mm});
            skLineSegment(sketch, "E11.5.1.4", {"start": v(19.4, 8.74) * mm, "end": v(17.4, 9.9) * mm});
            skLineSegment(sketch, "E11.5.1.5", {"start": v(17.4, 9.9) * mm, "end": v(17.4, 12.22) * mm});
            skLineSegment(sketch, "E11.5.2.0", {"start": v(18.38, 17.28) * mm, "end": v(20.39, 18.44) * mm});
            skLineSegment(sketch, "E11.5.2.1", {"start": v(20.39, 18.44) * mm, "end": v(22.4, 17.28) * mm});
            skLineSegment(sketch, "E11.5.2.2", {"start": v(22.4, 17.28) * mm, "end": v(22.4, 14.96) * mm});
            skLineSegment(sketch, "E11.5.2.3", {"start": v(22.4, 14.96) * mm, "end": v(20.39, 13.8) * mm});
            skLineSegment(sketch, "E11.5.2.4", {"start": v(20.39, 13.8) * mm, "end": v(18.38, 14.96) * mm});
            skLineSegment(sketch, "E11.5.2.5", {"start": v(18.38, 14.96) * mm, "end": v(18.38, 17.28) * mm});
            skLineSegment(sketch, "E11.5.3.0", {"start": v(19.36, 22.34) * mm, "end": v(21.36, 23.5) * mm});
            skLineSegment(sketch, "E11.5.3.1", {"start": v(21.36, 23.5) * mm, "end": v(23.37, 22.34) * mm});
            skLineSegment(sketch, "E11.5.3.2", {"start": v(23.37, 22.34) * mm, "end": v(23.37, 20.02) * mm});
            skLineSegment(sketch, "E11.5.3.3", {"start": v(23.37, 20.02) * mm, "end": v(21.36, 18.86) * mm});
            skLineSegment(sketch, "E11.5.3.4", {"start": v(21.36, 18.86) * mm, "end": v(19.36, 20.02) * mm});
            skLineSegment(sketch, "E11.5.3.5", {"start": v(19.36, 20.02) * mm, "end": v(19.36, 22.34) * mm});
            skLineSegment(sketch, "E11.5.4.0", {"start": v(20.33, 27.4) * mm, "end": v(22.34, 28.56) * mm});
            skLineSegment(sketch, "E11.5.4.1", {"start": v(22.34, 28.56) * mm, "end": v(24.35, 27.4) * mm});
            skLineSegment(sketch, "E11.5.4.2", {"start": v(24.35, 27.4) * mm, "end": v(24.35, 25.08) * mm});
            skLineSegment(sketch, "E11.5.4.3", {"start": v(24.35, 25.08) * mm, "end": v(22.34, 23.92) * mm});
            skLineSegment(sketch, "E11.5.4.4", {"start": v(22.34, 23.92) * mm, "end": v(20.33, 25.08) * mm});
            skLineSegment(sketch, "E11.5.4.5", {"start": v(20.33, 25.08) * mm, "end": v(20.33, 27.4) * mm});
            skLineSegment(sketch, "E11.5.5.0", {"start": v(21.31, 32.46) * mm, "end": v(23.32, 33.62) * mm});
            skLineSegment(sketch, "E11.5.5.1", {"start": v(23.32, 33.62) * mm, "end": v(25.33, 32.46) * mm});
            skLineSegment(sketch, "E11.5.5.2", {"start": v(25.33, 32.46) * mm, "end": v(25.33, 30.14) * mm});
            skLineSegment(sketch, "E11.5.5.3", {"start": v(25.33, 30.14) * mm, "end": v(23.32, 28.98) * mm});
            skLineSegment(sketch, "E11.5.5.4", {"start": v(23.32, 28.98) * mm, "end": v(21.31, 30.14) * mm});
            skLineSegment(sketch, "E11.5.5.5", {"start": v(21.31, 30.14) * mm, "end": v(21.31, 32.46) * mm});
            skLineSegment(sketch, "E11.5.6.0", {"start": v(22.3, 37.52) * mm, "end": v(24.3, 38.68) * mm});
            skLineSegment(sketch, "E11.5.6.1", {"start": v(24.3, 38.68) * mm, "end": v(26.3, 37.52) * mm});
            skLineSegment(sketch, "E11.5.6.2", {"start": v(26.3, 37.52) * mm, "end": v(26.3, 35.2) * mm});
            skLineSegment(sketch, "E11.5.6.3", {"start": v(26.3, 35.2) * mm, "end": v(24.3, 34.04) * mm});
            skLineSegment(sketch, "E11.5.6.4", {"start": v(24.3, 34.04) * mm, "end": v(22.3, 35.2) * mm});
            skLineSegment(sketch, "E11.5.6.5", {"start": v(22.3, 35.2) * mm, "end": v(22.3, 37.52) * mm});
            skLineSegment(sketch, "E11.5.7.0", {"start": v(23.27, 42.58) * mm, "end": v(25.28, 43.74) * mm});
            skLineSegment(sketch, "E11.5.7.1", {"start": v(25.28, 43.74) * mm, "end": v(27.29, 42.58) * mm});
            skLineSegment(sketch, "E11.5.7.2", {"start": v(27.29, 42.58) * mm, "end": v(27.29, 40.26) * mm});
            skLineSegment(sketch, "E11.5.7.3", {"start": v(27.29, 40.26) * mm, "end": v(25.28, 39.1) * mm});
            skLineSegment(sketch, "E11.5.7.4", {"start": v(25.28, 39.1) * mm, "end": v(23.27, 40.26) * mm});
            skLineSegment(sketch, "E11.5.7.5", {"start": v(23.27, 40.26) * mm, "end": v(23.27, 42.58) * mm});
            skLineSegment(sketch, "E11.5.8.0", {"start": v(24.25, 47.64) * mm, "end": v(26.26, 48.8) * mm});
            skLineSegment(sketch, "E11.5.8.1", {"start": v(26.26, 48.8) * mm, "end": v(28.26, 47.64) * mm});
            skLineSegment(sketch, "E11.5.8.2", {"start": v(28.26, 47.64) * mm, "end": v(28.26, 45.32) * mm});
            skLineSegment(sketch, "E11.5.8.3", {"start": v(28.26, 45.32) * mm, "end": v(26.26, 44.16) * mm});
            skLineSegment(sketch, "E11.5.8.4", {"start": v(26.26, 44.16) * mm, "end": v(24.25, 45.32) * mm});
            skLineSegment(sketch, "E11.5.8.5", {"start": v(24.25, 45.32) * mm, "end": v(24.25, 47.64) * mm});
            skLineSegment(sketch, "E11.5.9.0", {"start": v(25.23, 52.7) * mm, "end": v(27.23, 53.86) * mm});
            skLineSegment(sketch, "E11.5.9.1", {"start": v(27.23, 53.86) * mm, "end": v(29.24, 52.7) * mm});
            skLineSegment(sketch, "E11.5.9.2", {"start": v(29.24, 52.7) * mm, "end": v(29.24, 50.38) * mm});
            skLineSegment(sketch, "E11.5.9.3", {"start": v(29.24, 50.38) * mm, "end": v(27.23, 49.22) * mm});
            skLineSegment(sketch, "E11.5.9.4", {"start": v(27.23, 49.22) * mm, "end": v(25.23, 50.38) * mm});
            skLineSegment(sketch, "E11.5.9.5", {"start": v(25.23, 50.38) * mm, "end": v(25.23, 52.7) * mm});
            skLineSegment(sketch, "E11.6.0.0", {"start": v(23.52, 7.16) * mm, "end": v(25.53, 8.32) * mm});
            skLineSegment(sketch, "E11.6.0.1", {"start": v(25.53, 8.32) * mm, "end": v(27.54, 7.16) * mm});
            skLineSegment(sketch, "E11.6.0.2", {"start": v(27.54, 7.16) * mm, "end": v(27.54, 4.84) * mm});
            skLineSegment(sketch, "E11.6.0.3", {"start": v(27.54, 4.84) * mm, "end": v(25.53, 3.68) * mm});
            skLineSegment(sketch, "E11.6.0.4", {"start": v(25.53, 3.68) * mm, "end": v(23.52, 4.84) * mm});
            skLineSegment(sketch, "E11.6.0.5", {"start": v(23.52, 4.84) * mm, "end": v(23.52, 7.16) * mm});
            skLineSegment(sketch, "E11.6.1.0", {"start": v(24.5, 12.22) * mm, "end": v(26.5, 13.38) * mm});
            skLineSegment(sketch, "E11.6.1.1", {"start": v(26.5, 13.38) * mm, "end": v(28.52, 12.22) * mm});
            skLineSegment(sketch, "E11.6.1.2", {"start": v(28.52, 12.22) * mm, "end": v(28.52, 9.9) * mm});
            skLineSegment(sketch, "E11.6.1.3", {"start": v(28.52, 9.9) * mm, "end": v(26.5, 8.74) * mm});
            skLineSegment(sketch, "E11.6.1.4", {"start": v(26.5, 8.74) * mm, "end": v(24.5, 9.9) * mm});
            skLineSegment(sketch, "E11.6.1.5", {"start": v(24.5, 9.9) * mm, "end": v(24.5, 12.22) * mm});
            skLineSegment(sketch, "E11.6.2.0", {"start": v(25.48, 17.28) * mm, "end": v(27.49, 18.44) * mm});
            skLineSegment(sketch, "E11.6.2.1", {"start": v(27.49, 18.44) * mm, "end": v(29.5, 17.28) * mm});
            skLineSegment(sketch, "E11.6.2.2", {"start": v(29.5, 17.28) * mm, "end": v(29.5, 14.96) * mm});
            skLineSegment(sketch, "E11.6.2.3", {"start": v(29.5, 14.96) * mm, "end": v(27.49, 13.8) * mm});
            skLineSegment(sketch, "E11.6.2.4", {"start": v(27.49, 13.8) * mm, "end": v(25.48, 14.96) * mm});
            skLineSegment(sketch, "E11.6.2.5", {"start": v(25.48, 14.96) * mm, "end": v(25.48, 17.28) * mm});
            skLineSegment(sketch, "E11.6.3.0", {"start": v(26.46, 22.34) * mm, "end": v(28.46, 23.5) * mm});
            skLineSegment(sketch, "E11.6.3.1", {"start": v(28.46, 23.5) * mm, "end": v(30.47, 22.34) * mm});
            skLineSegment(sketch, "E11.6.3.2", {"start": v(30.47, 22.34) * mm, "end": v(30.47, 20.02) * mm});
            skLineSegment(sketch, "E11.6.3.3", {"start": v(30.47, 20.02) * mm, "end": v(28.46, 18.86) * mm});
            skLineSegment(sketch, "E11.6.3.4", {"start": v(28.46, 18.86) * mm, "end": v(26.46, 20.02) * mm});
            skLineSegment(sketch, "E11.6.3.5", {"start": v(26.46, 20.02) * mm, "end": v(26.46, 22.34) * mm});
            skLineSegment(sketch, "E11.6.4.0", {"start": v(27.43, 27.4) * mm, "end": v(29.44, 28.56) * mm});
            skLineSegment(sketch, "E11.6.4.1", {"start": v(29.44, 28.56) * mm, "end": v(31.45, 27.4) * mm});
            skLineSegment(sketch, "E11.6.4.2", {"start": v(31.45, 27.4) * mm, "end": v(31.45, 25.08) * mm});
            skLineSegment(sketch, "E11.6.4.3", {"start": v(31.45, 25.08) * mm, "end": v(29.44, 23.92) * mm});
            skLineSegment(sketch, "E11.6.4.4", {"start": v(29.44, 23.92) * mm, "end": v(27.43, 25.08) * mm});
            skLineSegment(sketch, "E11.6.4.5", {"start": v(27.43, 25.08) * mm, "end": v(27.43, 27.4) * mm});
            skLineSegment(sketch, "E11.6.5.0", {"start": v(28.41, 32.46) * mm, "end": v(30.42, 33.62) * mm});
            skLineSegment(sketch, "E11.6.5.1", {"start": v(30.42, 33.62) * mm, "end": v(32.43, 32.46) * mm});
            skLineSegment(sketch, "E11.6.5.2", {"start": v(32.43, 32.46) * mm, "end": v(32.43, 30.14) * mm});
            skLineSegment(sketch, "E11.6.5.3", {"start": v(32.43, 30.14) * mm, "end": v(30.42, 28.98) * mm});
            skLineSegment(sketch, "E11.6.5.4", {"start": v(30.42, 28.98) * mm, "end": v(28.41, 30.14) * mm});
            skLineSegment(sketch, "E11.6.5.5", {"start": v(28.41, 30.14) * mm, "end": v(28.41, 32.46) * mm});
            skLineSegment(sketch, "E11.6.6.0", {"start": v(29.4, 37.52) * mm, "end": v(31.4, 38.68) * mm});
            skLineSegment(sketch, "E11.6.6.1", {"start": v(31.4, 38.68) * mm, "end": v(33.4, 37.52) * mm});
            skLineSegment(sketch, "E11.6.6.2", {"start": v(33.4, 37.52) * mm, "end": v(33.4, 35.2) * mm});
            skLineSegment(sketch, "E11.6.6.3", {"start": v(33.4, 35.2) * mm, "end": v(31.4, 34.04) * mm});
            skLineSegment(sketch, "E11.6.6.4", {"start": v(31.4, 34.04) * mm, "end": v(29.4, 35.2) * mm});
            skLineSegment(sketch, "E11.6.6.5", {"start": v(29.4, 35.2) * mm, "end": v(29.4, 37.52) * mm});
            skLineSegment(sketch, "E11.6.7.0", {"start": v(30.37, 42.58) * mm, "end": v(32.38, 43.74) * mm});
            skLineSegment(sketch, "E11.6.7.1", {"start": v(32.38, 43.74) * mm, "end": v(34.39, 42.58) * mm});
            skLineSegment(sketch, "E11.6.7.2", {"start": v(34.39, 42.58) * mm, "end": v(34.39, 40.26) * mm});
            skLineSegment(sketch, "E11.6.7.3", {"start": v(34.39, 40.26) * mm, "end": v(32.38, 39.1) * mm});
            skLineSegment(sketch, "E11.6.7.4", {"start": v(32.38, 39.1) * mm, "end": v(30.37, 40.26) * mm});
            skLineSegment(sketch, "E11.6.7.5", {"start": v(30.37, 40.26) * mm, "end": v(30.37, 42.58) * mm});
            skLineSegment(sketch, "E11.6.8.0", {"start": v(31.35, 47.64) * mm, "end": v(33.36, 48.8) * mm});
            skLineSegment(sketch, "E11.6.8.1", {"start": v(33.36, 48.8) * mm, "end": v(35.36, 47.64) * mm});
            skLineSegment(sketch, "E11.6.8.2", {"start": v(35.36, 47.64) * mm, "end": v(35.36, 45.32) * mm});
            skLineSegment(sketch, "E11.6.8.3", {"start": v(35.36, 45.32) * mm, "end": v(33.36, 44.16) * mm});
            skLineSegment(sketch, "E11.6.8.4", {"start": v(33.36, 44.16) * mm, "end": v(31.35, 45.32) * mm});
            skLineSegment(sketch, "E11.6.8.5", {"start": v(31.35, 45.32) * mm, "end": v(31.35, 47.64) * mm});
            skLineSegment(sketch, "E11.6.9.0", {"start": v(32.33, 52.7) * mm, "end": v(34.33, 53.86) * mm});
            skLineSegment(sketch, "E11.6.9.1", {"start": v(34.33, 53.86) * mm, "end": v(36.34, 52.7) * mm});
            skLineSegment(sketch, "E11.6.9.2", {"start": v(36.34, 52.7) * mm, "end": v(36.34, 50.38) * mm});
            skLineSegment(sketch, "E11.6.9.3", {"start": v(36.34, 50.38) * mm, "end": v(34.33, 49.22) * mm});
            skLineSegment(sketch, "E11.6.9.4", {"start": v(34.33, 49.22) * mm, "end": v(32.33, 50.38) * mm});
            skLineSegment(sketch, "E11.6.9.5", {"start": v(32.33, 50.38) * mm, "end": v(32.33, 52.7) * mm});
            skLineSegment(sketch, "E11.7.0.0", {"start": v(30.62, 7.16) * mm, "end": v(32.63, 8.32) * mm});
            skLineSegment(sketch, "E11.7.0.1", {"start": v(32.63, 8.32) * mm, "end": v(34.64, 7.16) * mm});
            skLineSegment(sketch, "E11.7.0.2", {"start": v(34.64, 7.16) * mm, "end": v(34.64, 4.84) * mm});
            skLineSegment(sketch, "E11.7.0.3", {"start": v(34.64, 4.84) * mm, "end": v(32.63, 3.68) * mm});
            skLineSegment(sketch, "E11.7.0.4", {"start": v(32.63, 3.68) * mm, "end": v(30.62, 4.84) * mm});
            skLineSegment(sketch, "E11.7.0.5", {"start": v(30.62, 4.84) * mm, "end": v(30.62, 7.16) * mm});
            skLineSegment(sketch, "E11.7.1.0", {"start": v(31.6, 12.22) * mm, "end": v(33.6, 13.38) * mm});
            skLineSegment(sketch, "E11.7.1.1", {"start": v(33.6, 13.38) * mm, "end": v(35.62, 12.22) * mm});
            skLineSegment(sketch, "E11.7.1.2", {"start": v(35.62, 12.22) * mm, "end": v(35.62, 9.9) * mm});
            skLineSegment(sketch, "E11.7.1.3", {"start": v(35.62, 9.9) * mm, "end": v(33.6, 8.74) * mm});
            skLineSegment(sketch, "E11.7.1.4", {"start": v(33.6, 8.74) * mm, "end": v(31.6, 9.9) * mm});
            skLineSegment(sketch, "E11.7.1.5", {"start": v(31.6, 9.9) * mm, "end": v(31.6, 12.22) * mm});
            skLineSegment(sketch, "E11.7.2.0", {"start": v(32.58, 17.28) * mm, "end": v(34.59, 18.44) * mm});
            skLineSegment(sketch, "E11.7.2.1", {"start": v(34.59, 18.44) * mm, "end": v(36.6, 17.28) * mm});
            skLineSegment(sketch, "E11.7.2.2", {"start": v(36.6, 17.28) * mm, "end": v(36.6, 14.96) * mm});
            skLineSegment(sketch, "E11.7.2.3", {"start": v(36.6, 14.96) * mm, "end": v(34.59, 13.8) * mm});
            skLineSegment(sketch, "E11.7.2.4", {"start": v(34.59, 13.8) * mm, "end": v(32.58, 14.96) * mm});
            skLineSegment(sketch, "E11.7.2.5", {"start": v(32.58, 14.96) * mm, "end": v(32.58, 17.28) * mm});
            skLineSegment(sketch, "E11.7.3.0", {"start": v(33.56, 22.34) * mm, "end": v(35.56, 23.5) * mm});
            skLineSegment(sketch, "E11.7.3.1", {"start": v(35.56, 23.5) * mm, "end": v(37.57, 22.34) * mm});
            skLineSegment(sketch, "E11.7.3.2", {"start": v(37.57, 22.34) * mm, "end": v(37.57, 20.02) * mm});
            skLineSegment(sketch, "E11.7.3.3", {"start": v(37.57, 20.02) * mm, "end": v(35.56, 18.86) * mm});
            skLineSegment(sketch, "E11.7.3.4", {"start": v(35.56, 18.86) * mm, "end": v(33.56, 20.02) * mm});
            skLineSegment(sketch, "E11.7.3.5", {"start": v(33.56, 20.02) * mm, "end": v(33.56, 22.34) * mm});
            skLineSegment(sketch, "E11.7.4.0", {"start": v(34.53, 27.4) * mm, "end": v(36.54, 28.56) * mm});
            skLineSegment(sketch, "E11.7.4.1", {"start": v(36.54, 28.56) * mm, "end": v(38.55, 27.4) * mm});
            skLineSegment(sketch, "E11.7.4.2", {"start": v(38.55, 27.4) * mm, "end": v(38.55, 25.08) * mm});
            skLineSegment(sketch, "E11.7.4.3", {"start": v(38.55, 25.08) * mm, "end": v(36.54, 23.92) * mm});
            skLineSegment(sketch, "E11.7.4.4", {"start": v(36.54, 23.92) * mm, "end": v(34.53, 25.08) * mm});
            skLineSegment(sketch, "E11.7.4.5", {"start": v(34.53, 25.08) * mm, "end": v(34.53, 27.4) * mm});
            skLineSegment(sketch, "E11.7.5.0", {"start": v(35.51, 32.46) * mm, "end": v(37.52, 33.62) * mm});
            skLineSegment(sketch, "E11.7.5.1", {"start": v(37.52, 33.62) * mm, "end": v(39.53, 32.46) * mm});
            skLineSegment(sketch, "E11.7.5.2", {"start": v(39.53, 32.46) * mm, "end": v(39.53, 30.14) * mm});
            skLineSegment(sketch, "E11.7.5.3", {"start": v(39.53, 30.14) * mm, "end": v(37.52, 28.98) * mm});
            skLineSegment(sketch, "E11.7.5.4", {"start": v(37.52, 28.98) * mm, "end": v(35.51, 30.14) * mm});
            skLineSegment(sketch, "E11.7.5.5", {"start": v(35.51, 30.14) * mm, "end": v(35.51, 32.46) * mm});
            skLineSegment(sketch, "E11.7.6.0", {"start": v(36.5, 37.52) * mm, "end": v(38.5, 38.68) * mm});
            skLineSegment(sketch, "E11.7.6.1", {"start": v(38.5, 38.68) * mm, "end": v(40.5, 37.52) * mm});
            skLineSegment(sketch, "E11.7.6.2", {"start": v(40.5, 37.52) * mm, "end": v(40.5, 35.2) * mm});
            skLineSegment(sketch, "E11.7.6.3", {"start": v(40.5, 35.2) * mm, "end": v(38.5, 34.04) * mm});
            skLineSegment(sketch, "E11.7.6.4", {"start": v(38.5, 34.04) * mm, "end": v(36.5, 35.2) * mm});
            skLineSegment(sketch, "E11.7.6.5", {"start": v(36.5, 35.2) * mm, "end": v(36.5, 37.52) * mm});
            skLineSegment(sketch, "E11.7.7.0", {"start": v(37.47, 42.58) * mm, "end": v(39.48, 43.74) * mm});
            skLineSegment(sketch, "E11.7.7.1", {"start": v(39.48, 43.74) * mm, "end": v(41.49, 42.58) * mm});
            skLineSegment(sketch, "E11.7.7.2", {"start": v(41.49, 42.58) * mm, "end": v(41.49, 40.26) * mm});
            skLineSegment(sketch, "E11.7.7.3", {"start": v(41.49, 40.26) * mm, "end": v(39.48, 39.1) * mm});
            skLineSegment(sketch, "E11.7.7.4", {"start": v(39.48, 39.1) * mm, "end": v(37.47, 40.26) * mm});
            skLineSegment(sketch, "E11.7.7.5", {"start": v(37.47, 40.26) * mm, "end": v(37.47, 42.58) * mm});
            skLineSegment(sketch, "E11.7.8.0", {"start": v(38.45, 47.64) * mm, "end": v(40.46, 48.8) * mm});
            skLineSegment(sketch, "E11.7.8.1", {"start": v(40.46, 48.8) * mm, "end": v(42.46, 47.64) * mm});
            skLineSegment(sketch, "E11.7.8.2", {"start": v(42.46, 47.64) * mm, "end": v(42.46, 45.32) * mm});
            skLineSegment(sketch, "E11.7.8.3", {"start": v(42.46, 45.32) * mm, "end": v(40.46, 44.16) * mm});
            skLineSegment(sketch, "E11.7.8.4", {"start": v(40.46, 44.16) * mm, "end": v(38.45, 45.32) * mm});
            skLineSegment(sketch, "E11.7.8.5", {"start": v(38.45, 45.32) * mm, "end": v(38.45, 47.64) * mm});
            skLineSegment(sketch, "E11.7.9.0", {"start": v(39.43, 52.7) * mm, "end": v(41.43, 53.86) * mm});
            skLineSegment(sketch, "E11.7.9.1", {"start": v(41.43, 53.86) * mm, "end": v(43.44, 52.7) * mm});
            skLineSegment(sketch, "E11.7.9.2", {"start": v(43.44, 52.7) * mm, "end": v(43.44, 50.38) * mm});
            skLineSegment(sketch, "E11.7.9.3", {"start": v(43.44, 50.38) * mm, "end": v(41.43, 49.22) * mm});
            skLineSegment(sketch, "E11.7.9.4", {"start": v(41.43, 49.22) * mm, "end": v(39.43, 50.38) * mm});
            skLineSegment(sketch, "E11.7.9.5", {"start": v(39.43, 50.38) * mm, "end": v(39.43, 52.7) * mm});
            skLineSegment(sketch, "E11.8.0.0", {"start": v(37.72, 7.16) * mm, "end": v(39.73, 8.32) * mm});
            skLineSegment(sketch, "E11.8.0.1", {"start": v(39.73, 8.32) * mm, "end": v(41.74, 7.16) * mm});
            skLineSegment(sketch, "E11.8.0.2", {"start": v(41.74, 7.16) * mm, "end": v(41.74, 4.84) * mm});
            skLineSegment(sketch, "E11.8.0.3", {"start": v(41.74, 4.84) * mm, "end": v(39.73, 3.68) * mm});
            skLineSegment(sketch, "E11.8.0.4", {"start": v(39.73, 3.68) * mm, "end": v(37.72, 4.84) * mm});
            skLineSegment(sketch, "E11.8.0.5", {"start": v(37.72, 4.84) * mm, "end": v(37.72, 7.16) * mm});
            skLineSegment(sketch, "E11.8.1.0", {"start": v(38.7, 12.22) * mm, "end": v(40.7, 13.38) * mm});
            skLineSegment(sketch, "E11.8.1.1", {"start": v(40.7, 13.38) * mm, "end": v(42.72, 12.22) * mm});
            skLineSegment(sketch, "E11.8.1.2", {"start": v(42.72, 12.22) * mm, "end": v(42.72, 9.9) * mm});
            skLineSegment(sketch, "E11.8.1.3", {"start": v(42.72, 9.9) * mm, "end": v(40.7, 8.74) * mm});
            skLineSegment(sketch, "E11.8.1.4", {"start": v(40.7, 8.74) * mm, "end": v(38.7, 9.9) * mm});
            skLineSegment(sketch, "E11.8.1.5", {"start": v(38.7, 9.9) * mm, "end": v(38.7, 12.22) * mm});
            skLineSegment(sketch, "E11.8.2.0", {"start": v(39.68, 17.28) * mm, "end": v(41.69, 18.44) * mm});
            skLineSegment(sketch, "E11.8.2.1", {"start": v(41.69, 18.44) * mm, "end": v(43.7, 17.28) * mm});
            skLineSegment(sketch, "E11.8.2.2", {"start": v(43.7, 17.28) * mm, "end": v(43.7, 14.96) * mm});
            skLineSegment(sketch, "E11.8.2.3", {"start": v(43.7, 14.96) * mm, "end": v(41.69, 13.8) * mm});
            skLineSegment(sketch, "E11.8.2.4", {"start": v(41.69, 13.8) * mm, "end": v(39.68, 14.96) * mm});
            skLineSegment(sketch, "E11.8.2.5", {"start": v(39.68, 14.96) * mm, "end": v(39.68, 17.28) * mm});
            skLineSegment(sketch, "E11.8.3.0", {"start": v(40.66, 22.34) * mm, "end": v(42.66, 23.5) * mm});
            skLineSegment(sketch, "E11.8.3.1", {"start": v(42.66, 23.5) * mm, "end": v(44.67, 22.34) * mm});
            skLineSegment(sketch, "E11.8.3.2", {"start": v(44.67, 22.34) * mm, "end": v(44.67, 20.02) * mm});
            skLineSegment(sketch, "E11.8.3.3", {"start": v(44.67, 20.02) * mm, "end": v(42.66, 18.86) * mm});
            skLineSegment(sketch, "E11.8.3.4", {"start": v(42.66, 18.86) * mm, "end": v(40.66, 20.02) * mm});
            skLineSegment(sketch, "E11.8.3.5", {"start": v(40.66, 20.02) * mm, "end": v(40.66, 22.34) * mm});
            skLineSegment(sketch, "E11.8.4.0", {"start": v(41.63, 27.4) * mm, "end": v(43.64, 28.56) * mm});
            skLineSegment(sketch, "E11.8.4.1", {"start": v(43.64, 28.56) * mm, "end": v(45.65, 27.4) * mm});
            skLineSegment(sketch, "E11.8.4.2", {"start": v(45.65, 27.4) * mm, "end": v(45.65, 25.08) * mm});
            skLineSegment(sketch, "E11.8.4.3", {"start": v(45.65, 25.08) * mm, "end": v(43.64, 23.92) * mm});
            skLineSegment(sketch, "E11.8.4.4", {"start": v(43.64, 23.92) * mm, "end": v(41.63, 25.08) * mm});
            skLineSegment(sketch, "E11.8.4.5", {"start": v(41.63, 25.08) * mm, "end": v(41.63, 27.4) * mm});
            skLineSegment(sketch, "E11.8.5.0", {"start": v(42.61, 32.46) * mm, "end": v(44.62, 33.62) * mm});
            skLineSegment(sketch, "E11.8.5.1", {"start": v(44.62, 33.62) * mm, "end": v(46.63, 32.46) * mm});
            skLineSegment(sketch, "E11.8.5.2", {"start": v(46.63, 32.46) * mm, "end": v(46.63, 30.14) * mm});
            skLineSegment(sketch, "E11.8.5.3", {"start": v(46.63, 30.14) * mm, "end": v(44.62, 28.98) * mm});
            skLineSegment(sketch, "E11.8.5.4", {"start": v(44.62, 28.98) * mm, "end": v(42.61, 30.14) * mm});
            skLineSegment(sketch, "E11.8.5.5", {"start": v(42.61, 30.14) * mm, "end": v(42.61, 32.46) * mm});
            skLineSegment(sketch, "E11.8.6.0", {"start": v(43.6, 37.52) * mm, "end": v(45.6, 38.68) * mm});
            skLineSegment(sketch, "E11.8.6.1", {"start": v(45.6, 38.68) * mm, "end": v(47.6, 37.52) * mm});
            skLineSegment(sketch, "E11.8.6.2", {"start": v(47.6, 37.52) * mm, "end": v(47.6, 35.2) * mm});
            skLineSegment(sketch, "E11.8.6.3", {"start": v(47.6, 35.2) * mm, "end": v(45.6, 34.04) * mm});
            skLineSegment(sketch, "E11.8.6.4", {"start": v(45.6, 34.04) * mm, "end": v(43.6, 35.2) * mm});
            skLineSegment(sketch, "E11.8.6.5", {"start": v(43.6, 35.2) * mm, "end": v(43.6, 37.52) * mm});
            skLineSegment(sketch, "E11.8.7.0", {"start": v(44.57, 42.58) * mm, "end": v(46.58, 43.74) * mm});
            skLineSegment(sketch, "E11.8.7.1", {"start": v(46.58, 43.74) * mm, "end": v(48.59, 42.58) * mm});
            skLineSegment(sketch, "E11.8.7.2", {"start": v(48.59, 42.58) * mm, "end": v(48.59, 40.26) * mm});
            skLineSegment(sketch, "E11.8.7.3", {"start": v(48.59, 40.26) * mm, "end": v(46.58, 39.1) * mm});
            skLineSegment(sketch, "E11.8.7.4", {"start": v(46.58, 39.1) * mm, "end": v(44.57, 40.26) * mm});
            skLineSegment(sketch, "E11.8.7.5", {"start": v(44.57, 40.26) * mm, "end": v(44.57, 42.58) * mm});
            skLineSegment(sketch, "E11.8.8.0", {"start": v(45.55, 47.64) * mm, "end": v(47.56, 48.8) * mm});
            skLineSegment(sketch, "E11.8.8.1", {"start": v(47.56, 48.8) * mm, "end": v(49.56, 47.64) * mm});
            skLineSegment(sketch, "E11.8.8.2", {"start": v(49.56, 47.64) * mm, "end": v(49.56, 45.32) * mm});
            skLineSegment(sketch, "E11.8.8.3", {"start": v(49.56, 45.32) * mm, "end": v(47.56, 44.16) * mm});
            skLineSegment(sketch, "E11.8.8.4", {"start": v(47.56, 44.16) * mm, "end": v(45.55, 45.32) * mm});
            skLineSegment(sketch, "E11.8.8.5", {"start": v(45.55, 45.32) * mm, "end": v(45.55, 47.64) * mm});
            skLineSegment(sketch, "E11.8.9.0", {"start": v(46.53, 52.7) * mm, "end": v(48.53, 53.86) * mm});
            skLineSegment(sketch, "E11.8.9.1", {"start": v(48.53, 53.86) * mm, "end": v(50.54, 52.7) * mm});
            skLineSegment(sketch, "E11.8.9.2", {"start": v(50.54, 52.7) * mm, "end": v(50.54, 50.38) * mm});
            skLineSegment(sketch, "E11.8.9.3", {"start": v(50.54, 50.38) * mm, "end": v(48.53, 49.22) * mm});
            skLineSegment(sketch, "E11.8.9.4", {"start": v(48.53, 49.22) * mm, "end": v(46.53, 50.38) * mm});
            skLineSegment(sketch, "E11.8.9.5", {"start": v(46.53, 50.38) * mm, "end": v(46.53, 52.7) * mm});
            skLineSegment(sketch, "E11.9.0.0", {"start": v(44.82, 7.16) * mm, "end": v(46.83, 8.32) * mm});
            skLineSegment(sketch, "E11.9.0.1", {"start": v(46.83, 8.32) * mm, "end": v(48.84, 7.16) * mm});
            skLineSegment(sketch, "E11.9.0.2", {"start": v(48.84, 7.16) * mm, "end": v(48.84, 4.84) * mm});
            skLineSegment(sketch, "E11.9.0.3", {"start": v(48.84, 4.84) * mm, "end": v(46.83, 3.68) * mm});
            skLineSegment(sketch, "E11.9.0.4", {"start": v(46.83, 3.68) * mm, "end": v(44.82, 4.84) * mm});
            skLineSegment(sketch, "E11.9.0.5", {"start": v(44.82, 4.84) * mm, "end": v(44.82, 7.16) * mm});
            skLineSegment(sketch, "E11.9.1.0", {"start": v(45.8, 12.22) * mm, "end": v(47.8, 13.38) * mm});
            skLineSegment(sketch, "E11.9.1.1", {"start": v(47.8, 13.38) * mm, "end": v(49.82, 12.22) * mm});
            skLineSegment(sketch, "E11.9.1.2", {"start": v(49.82, 12.22) * mm, "end": v(49.82, 9.9) * mm});
            skLineSegment(sketch, "E11.9.1.3", {"start": v(49.82, 9.9) * mm, "end": v(47.8, 8.74) * mm});
            skLineSegment(sketch, "E11.9.1.4", {"start": v(47.8, 8.74) * mm, "end": v(45.8, 9.9) * mm});
            skLineSegment(sketch, "E11.9.1.5", {"start": v(45.8, 9.9) * mm, "end": v(45.8, 12.22) * mm});
            skLineSegment(sketch, "E11.9.2.0", {"start": v(46.78, 17.28) * mm, "end": v(48.79, 18.44) * mm});
            skLineSegment(sketch, "E11.9.2.1", {"start": v(48.79, 18.44) * mm, "end": v(50.8, 17.28) * mm});
            skLineSegment(sketch, "E11.9.2.2", {"start": v(50.8, 17.28) * mm, "end": v(50.8, 14.96) * mm});
            skLineSegment(sketch, "E11.9.2.3", {"start": v(50.8, 14.96) * mm, "end": v(48.79, 13.8) * mm});
            skLineSegment(sketch, "E11.9.2.4", {"start": v(48.79, 13.8) * mm, "end": v(46.78, 14.96) * mm});
            skLineSegment(sketch, "E11.9.2.5", {"start": v(46.78, 14.96) * mm, "end": v(46.78, 17.28) * mm});
            skLineSegment(sketch, "E11.9.3.0", {"start": v(47.76, 22.34) * mm, "end": v(49.76, 23.5) * mm});
            skLineSegment(sketch, "E11.9.3.1", {"start": v(49.76, 23.5) * mm, "end": v(51.77, 22.34) * mm});
            skLineSegment(sketch, "E11.9.3.2", {"start": v(51.77, 22.34) * mm, "end": v(51.77, 20.02) * mm});
            skLineSegment(sketch, "E11.9.3.3", {"start": v(51.77, 20.02) * mm, "end": v(49.76, 18.86) * mm});
            skLineSegment(sketch, "E11.9.3.4", {"start": v(49.76, 18.86) * mm, "end": v(47.76, 20.02) * mm});
            skLineSegment(sketch, "E11.9.3.5", {"start": v(47.76, 20.02) * mm, "end": v(47.76, 22.34) * mm});
            skLineSegment(sketch, "E11.9.4.0", {"start": v(48.73, 27.4) * mm, "end": v(50.74, 28.56) * mm});
            skLineSegment(sketch, "E11.9.4.1", {"start": v(50.74, 28.56) * mm, "end": v(52.75, 27.4) * mm});
            skLineSegment(sketch, "E11.9.4.2", {"start": v(52.75, 27.4) * mm, "end": v(52.75, 25.08) * mm});
            skLineSegment(sketch, "E11.9.4.3", {"start": v(52.75, 25.08) * mm, "end": v(50.74, 23.92) * mm});
            skLineSegment(sketch, "E11.9.4.4", {"start": v(50.74, 23.92) * mm, "end": v(48.73, 25.08) * mm});
            skLineSegment(sketch, "E11.9.4.5", {"start": v(48.73, 25.08) * mm, "end": v(48.73, 27.4) * mm});
            skLineSegment(sketch, "E11.9.5.0", {"start": v(49.71, 32.46) * mm, "end": v(51.72, 33.62) * mm});
            skLineSegment(sketch, "E11.9.5.1", {"start": v(51.72, 33.62) * mm, "end": v(53.73, 32.46) * mm});
            skLineSegment(sketch, "E11.9.5.2", {"start": v(53.73, 32.46) * mm, "end": v(53.73, 30.14) * mm});
            skLineSegment(sketch, "E11.9.5.3", {"start": v(53.73, 30.14) * mm, "end": v(51.72, 28.98) * mm});
            skLineSegment(sketch, "E11.9.5.4", {"start": v(51.72, 28.98) * mm, "end": v(49.71, 30.14) * mm});
            skLineSegment(sketch, "E11.9.5.5", {"start": v(49.71, 30.14) * mm, "end": v(49.71, 32.46) * mm});
            skLineSegment(sketch, "E11.9.6.0", {"start": v(50.7, 37.52) * mm, "end": v(52.7, 38.68) * mm});
            skLineSegment(sketch, "E11.9.6.1", {"start": v(52.7, 38.68) * mm, "end": v(54.7, 37.52) * mm});
            skLineSegment(sketch, "E11.9.6.2", {"start": v(54.7, 37.52) * mm, "end": v(54.7, 35.2) * mm});
            skLineSegment(sketch, "E11.9.6.3", {"start": v(54.7, 35.2) * mm, "end": v(52.7, 34.04) * mm});
            skLineSegment(sketch, "E11.9.6.4", {"start": v(52.7, 34.04) * mm, "end": v(50.7, 35.2) * mm});
            skLineSegment(sketch, "E11.9.6.5", {"start": v(50.7, 35.2) * mm, "end": v(50.7, 37.52) * mm});
            skLineSegment(sketch, "E11.9.7.0", {"start": v(51.67, 42.58) * mm, "end": v(53.68, 43.74) * mm});
            skLineSegment(sketch, "E11.9.7.1", {"start": v(53.68, 43.74) * mm, "end": v(55.69, 42.58) * mm});
            skLineSegment(sketch, "E11.9.7.2", {"start": v(55.69, 42.58) * mm, "end": v(55.69, 40.26) * mm});
            skLineSegment(sketch, "E11.9.7.3", {"start": v(55.69, 40.26) * mm, "end": v(53.68, 39.1) * mm});
            skLineSegment(sketch, "E11.9.7.4", {"start": v(53.68, 39.1) * mm, "end": v(51.67, 40.26) * mm});
            skLineSegment(sketch, "E11.9.7.5", {"start": v(51.67, 40.26) * mm, "end": v(51.67, 42.58) * mm});
            skLineSegment(sketch, "E11.9.8.0", {"start": v(52.65, 47.64) * mm, "end": v(54.66, 48.8) * mm});
            skLineSegment(sketch, "E11.9.8.1", {"start": v(54.66, 48.8) * mm, "end": v(56.66, 47.64) * mm});
            skLineSegment(sketch, "E11.9.8.2", {"start": v(56.66, 47.64) * mm, "end": v(56.66, 45.32) * mm});
            skLineSegment(sketch, "E11.9.8.3", {"start": v(56.66, 45.32) * mm, "end": v(54.66, 44.16) * mm});
            skLineSegment(sketch, "E11.9.8.4", {"start": v(54.66, 44.16) * mm, "end": v(52.65, 45.32) * mm});
            skLineSegment(sketch, "E11.9.8.5", {"start": v(52.65, 45.32) * mm, "end": v(52.65, 47.64) * mm});
            skLineSegment(sketch, "E11.9.9.0", {"start": v(53.63, 52.7) * mm, "end": v(55.63, 53.86) * mm});
            skLineSegment(sketch, "E11.9.9.1", {"start": v(55.63, 53.86) * mm, "end": v(57.64, 52.7) * mm});
            skLineSegment(sketch, "E11.9.9.2", {"start": v(57.64, 52.7) * mm, "end": v(57.64, 50.38) * mm});
            skLineSegment(sketch, "E11.9.9.3", {"start": v(57.64, 50.38) * mm, "end": v(55.63, 49.22) * mm});
            skLineSegment(sketch, "E11.9.9.4", {"start": v(55.63, 49.22) * mm, "end": v(53.63, 50.38) * mm});
            skLineSegment(sketch, "E11.9.9.5", {"start": v(53.63, 50.38) * mm, "end": v(53.63, 52.7) * mm});
            skLineSegment(sketch, "E11.direction1", {"start": v(-19.08, 4.84) * mm, "end": v(-11.98, 4.84) * mm, "construction": true});
            skLineSegment(sketch, "E11.direction2", {"start": v(-19.08, 4.84) * mm, "end": v(-18.1, 9.9) * mm, "construction": true});
            skLineSegment(sketch, "E12", {"start": v(-45.68, 26.97) * mm, "end": v(-26.48, 26.97) * mm});
            skLineSegment(sketch, "E13", {"start": v(-26.48, 26.97) * mm, "end": v(-26.48, 35.97) * mm});
            skLineSegment(sketch, "E14", {"start": v(-45.68, 35.97) * mm, "end": v(-45.68, 26.97) * mm});
            skLineSegment(sketch, "E15.bottom", {"start": v(-40.32, 29.43) * mm, "end": v(-39.53, 29.43) * mm});
            skLineSegment(sketch, "E15.top", {"start": v(-40.32, 32.04) * mm, "end": v(-39.53, 32.04) * mm});
            skLineSegment(sketch, "E15.left", {"start": v(-40.32, 29.43) * mm, "end": v(-40.32, 32.04) * mm});
            skLineSegment(sketch, "E15.right", {"start": v(-39.53, 29.43) * mm, "end": v(-39.53, 32.04) * mm});
            skLineSegment(sketch, "E16", {"start": v(-45.68, 35.97) * mm, "end": v(-42.56, 39.6) * mm});
            skLineSegment(sketch, "E17", {"start": v(-26.48, 35.97) * mm, "end": v(-29.6, 39.6) * mm});
            skPoint(sketch, "E18", {"position": v(-29.6, 39.6) * mm});
            skLineSegment(sketch, "E19", {"start": v(-42.56, 39.6) * mm, "end": v(-29.6, 39.6) * mm});
            skLineSegment(sketch, "E20.bottom", {"start": v(-32.1, 29.37) * mm, "end": v(-31.3, 29.37) * mm});
            skLineSegment(sketch, "E20.top", {"start": v(-32.1, 31.97) * mm, "end": v(-31.3, 31.97) * mm});
            skLineSegment(sketch, "E20.left", {"start": v(-32.1, 29.37) * mm, "end": v(-32.1, 31.97) * mm});
            skLineSegment(sketch, "E20.right", {"start": v(-31.3, 29.37) * mm, "end": v(-31.3, 31.97) * mm});
            skLineSegment(sketch, "E21.bottom", {"start": v(-36.42, 33.25) * mm, "end": v(-35.63, 33.25) * mm});
            skLineSegment(sketch, "E21.top", {"start": v(-36.42, 35.86) * mm, "end": v(-35.63, 35.86) * mm});
            skLineSegment(sketch, "E21.left", {"start": v(-36.42, 33.25) * mm, "end": v(-36.42, 35.86) * mm});
            skLineSegment(sketch, "E21.right", {"start": v(-35.63, 33.25) * mm, "end": v(-35.63, 35.86) * mm});
            skPoint(sketch, "E22", {"position": v(-36.08, 39.6) * mm});
            skPoint(sketch, "E23", {"position": v(-36.08, 35.84) * mm});
            skLineSegment(sketch, "E24.bottom", {"start": v(-47.54, 19.58) * mm, "end": v(-36.54, 19.58) * mm});
            skLineSegment(sketch, "E24.top", {"start": v(-47.54, 12.58) * mm, "end": v(-36.54, 12.58) * mm});
            skLineSegment(sketch, "E24.left", {"start": v(-47.54, 19.58) * mm, "end": v(-47.54, 12.58) * mm});
            skLineSegment(sketch, "E24.right", {"start": v(-36.54, 19.58) * mm, "end": v(-36.54, 12.58) * mm});
            skSolve(sketch);
        }
        {
            var Q0;
            Q0=sQuery(id+"F2.wireOp",VERTEX,"E2");
            var Q1;
            Q1=sQuery(id+"F2.wireOp",VERTEX,"E1");
            var Q2;
            Q2=sQuery(id+"F2.wireOp",VERTEX,"E3");
            var Q3;
            Q3=sQuery(id+"F2.wireOp",VERTEX,"E4");
            var Q4;
            Q4=sQuery(id+"F2.wireOp",VERTEX,"E5");
            var Q5;
            Q5=sQuery(id+"F2.wireOp",VERTEX,"E6");
            var Q6;
            Q6=makeQuery(id+"F1.opExtrude","SWEPT_BODY",BODY,{"disambiguationData":[OSD([sQuery(id+"F0.wireOp",EDGE,"E0.bottom"),sQuery(id+"F0.wireOp",EDGE,"E0.top"),sQuery(id+"F0.wireOp",EDGE,"E0.left"),sQuery(id+"F0.wireOp",EDGE,"E0.right")])]});
            hole(context, id + "F3", {"style" : HoleStyle.SIMPLE, "endStyle" : HoleEndStyle.BLIND, "standardTappedOrClearance" : lookupTablePath({ "standard" : "ANSI", "fit" : "Normal (ASME)", "size" : "#6", "type" : "Clearance" }), "standardBlindInLast" : lookupTablePath({ "fit" : "Free", "standard" : "ANSI", "size" : "#6", "type" : "Clearance" }), "holeDiameter" : 3.8 * mm, "holeDepth" : 15.8 * mm, "isTappedThrough" : true, "tappedDepth" : 12 * mm, "tapClearance" : 3, "locations" : qUnion([Q0, Q1, Q2, Q3, Q4, Q5]), "scope" : qUnion([Q6])});
        }
        {
            var Q0;
            Q0=makeQuery(id+"F2.imprint","IMPRINT",FACE,{"disambiguationData":[TD([[makeQuery(id+"F2.imprint","IMPRINT",EDGE,{"derivedFrom":sQuery(id+"F2.wireOp",EDGE,"E7.bottom")}),-1.0]])]});
            var Q1;
            Q1=makeQuery(id+"F2.imprint","IMPRINT",FACE,{"disambiguationData":[TD([[makeQuery(id+"F2.imprint","IMPRINT",EDGE,{"derivedFrom":sQuery(id+"F2.wireOp",EDGE,"E8.bottom")}),1.0]])]});
            extrude(context, id + "F4", {"entities" : qUnion([Q0, Q1]), "operationType" : NewBodyOperationType.ADD, "depth" : 2 * mm, "offsetDistance" : 25 * mm});
        }
        {
            var Q0;
            Q0=makeQuery(id+"F2.imprint","IMPRINT",FACE,{"disambiguationData":[TD([[makeQuery(id+"F2.imprint","IMPRINT",EDGE,{"derivedFrom":sQuery(id+"F2.wireOp",EDGE,"E12")}),1.0]])]});
            extrude(context, id + "F5", {"entities" : qUnion([Q0]), "operationType" : NewBodyOperationType.REMOVE, "oppositeDirection" : true, "depth" : 10 * mm, "offsetDistance" : 25 * mm});
        }
        {
            var Q0;
            {var subQ1=sQuery(id+"F2.wireOp",EDGE,"E11.9.0.3");Q0=makeQuery(id+"F2.imprint","IMPRINT",FACE,{"disambiguationData":[TD([[makeQuery(id+"F2.imprint","IMPRINT",EDGE,{"derivedFrom":subQ1}),-1.0]])]});}
            var Q1;
            {var subQ6=sQuery(id+"F2.wireOp",EDGE,"E11.9.0.0");Q1=makeQuery(id+"F2.imprint","IMPRINT",FACE,{"disambiguationData":[TD([[makeQuery(id+"F2.imprint","IMPRINT",EDGE,{"derivedFrom":subQ6}),-1.0]])]});}
            var Q2;
            Q2=makeQuery(id+"F2.imprint","IMPRINT",FACE,{"disambiguationData":[TD([[makeQuery(id+"F2.imprint","IMPRINT",EDGE,{"derivedFrom":sQuery(id+"F2.wireOp",EDGE,"E11.9.1.0")}),-1.0]])]});
            var Q3;
            Q3=makeQuery(id+"F2.imprint","IMPRINT",FACE,{"disambiguationData":[TD([[makeQuery(id+"F2.imprint","IMPRINT",EDGE,{"derivedFrom":sQuery(id+"F2.wireOp",EDGE,"E11.9.2.0")}),-1.0]])]});
            var Q4;
            Q4=makeQuery(id+"F2.imprint","IMPRINT",FACE,{"disambiguationData":[TD([[makeQuery(id+"F2.imprint","IMPRINT",EDGE,{"derivedFrom":sQuery(id+"F2.wireOp",EDGE,"E11.9.3.0")}),-1.0]])]});
            var Q5;
            Q5=makeQuery(id+"F2.imprint","IMPRINT",FACE,{"disambiguationData":[TD([[makeQuery(id+"F2.imprint","IMPRINT",EDGE,{"derivedFrom":sQuery(id+"F2.wireOp",EDGE,"E11.9.4.0")}),-1.0]])]});
            var Q6;
            Q6=makeQuery(id+"F2.imprint","IMPRINT",FACE,{"disambiguationData":[TD([[makeQuery(id+"F2.imprint","IMPRINT",EDGE,{"derivedFrom":sQuery(id+"F2.wireOp",EDGE,"E11.9.5.0")}),-1.0]])]});
            var Q7;
            Q7=makeQuery(id+"F2.imprint","IMPRINT",FACE,{"disambiguationData":[TD([[makeQuery(id+"F2.imprint","IMPRINT",EDGE,{"derivedFrom":sQuery(id+"F2.wireOp",EDGE,"E11.9.6.0")}),-1.0]])]});
            var Q8;
            Q8=makeQuery(id+"F2.imprint","IMPRINT",FACE,{"disambiguationData":[TD([[makeQuery(id+"F2.imprint","IMPRINT",EDGE,{"derivedFrom":sQuery(id+"F2.wireOp",EDGE,"E11.9.7.0")}),-1.0]])]});
            var Q9;
            Q9=makeQuery(id+"F2.imprint","IMPRINT",FACE,{"disambiguationData":[TD([[makeQuery(id+"F2.imprint","IMPRINT",EDGE,{"derivedFrom":sQuery(id+"F2.wireOp",EDGE,"E11.9.8.0")}),-1.0]])]});
            var Q10;
            Q10=makeQuery(id+"F2.imprint","IMPRINT",FACE,{"disambiguationData":[TD([[makeQuery(id+"F2.imprint","IMPRINT",EDGE,{"derivedFrom":sQuery(id+"F2.wireOp",EDGE,"E11.9.9.0")}),-1.0]])]});
            var Q11;
            {var subQ1=sQuery(id+"F2.wireOp",EDGE,"E11.8.0.0");Q11=makeQuery(id+"F2.imprint","IMPRINT",FACE,{"disambiguationData":[TD([[makeQuery(id+"F2.imprint","IMPRINT",EDGE,{"derivedFrom":subQ1}),-1.0]])]});}
            var Q12;
            {var subQ1=sQuery(id+"F2.wireOp",EDGE,"E11.8.0.3");Q12=makeQuery(id+"F2.imprint","IMPRINT",FACE,{"disambiguationData":[TD([[makeQuery(id+"F2.imprint","IMPRINT",EDGE,{"derivedFrom":subQ1}),-1.0]])]});}
            var Q13;
            {var subQ1=sQuery(id+"F2.wireOp",EDGE,"E11.7.0.3");Q13=makeQuery(id+"F2.imprint","IMPRINT",FACE,{"disambiguationData":[TD([[makeQuery(id+"F2.imprint","IMPRINT",EDGE,{"derivedFrom":subQ1}),-1.0]])]});}
            var Q14;
            {var subQ4=sQuery(id+"F2.wireOp",EDGE,"E11.7.0.0");Q14=makeQuery(id+"F2.imprint","IMPRINT",FACE,{"disambiguationData":[TD([[makeQuery(id+"F2.imprint","IMPRINT",EDGE,{"derivedFrom":subQ4}),-1.0]])]});}
            var Q15;
            {var subQ4=sQuery(id+"F2.wireOp",EDGE,"E11.6.0.0");Q15=makeQuery(id+"F2.imprint","IMPRINT",FACE,{"disambiguationData":[TD([[makeQuery(id+"F2.imprint","IMPRINT",EDGE,{"derivedFrom":subQ4}),-1.0]])]});}
            var Q16;
            {var subQ1=sQuery(id+"F2.wireOp",EDGE,"E11.6.0.3");Q16=makeQuery(id+"F2.imprint","IMPRINT",FACE,{"disambiguationData":[TD([[makeQuery(id+"F2.imprint","IMPRINT",EDGE,{"derivedFrom":subQ1}),-1.0]])]});}
            var Q17;
            {var subQ0=sQuery(id+"F2.wireOp",EDGE,"E11.5.0.3");Q17=makeQuery(id+"F2.imprint","IMPRINT",FACE,{"disambiguationData":[TD([[makeQuery(id+"F2.imprint","IMPRINT",EDGE,{"derivedFrom":subQ0}),-1.0]])]});}
            var Q18;
            {var subQ4=sQuery(id+"F2.wireOp",EDGE,"E11.5.0.0");Q18=makeQuery(id+"F2.imprint","IMPRINT",FACE,{"disambiguationData":[TD([[makeQuery(id+"F2.imprint","IMPRINT",EDGE,{"derivedFrom":subQ4}),-1.0]])]});}
            var Q19;
            {var subQ4=sQuery(id+"F2.wireOp",EDGE,"E11.4.0.0");Q19=makeQuery(id+"F2.imprint","IMPRINT",FACE,{"disambiguationData":[TD([[makeQuery(id+"F2.imprint","IMPRINT",EDGE,{"derivedFrom":subQ4}),-1.0]])]});}
            var Q20;
            {var subQ1=sQuery(id+"F2.wireOp",EDGE,"E11.4.0.3");Q20=makeQuery(id+"F2.imprint","IMPRINT",FACE,{"disambiguationData":[TD([[makeQuery(id+"F2.imprint","IMPRINT",EDGE,{"derivedFrom":subQ1}),-1.0]])]});}
            var Q21;
            {var subQ6=sQuery(id+"F2.wireOp",EDGE,"E11.3.0.3");Q21=makeQuery(id+"F2.imprint","IMPRINT",FACE,{"disambiguationData":[TD([[makeQuery(id+"F2.imprint","IMPRINT",EDGE,{"derivedFrom":subQ6}),-1.0]])]});}
            var Q22;
            {var subQ1=sQuery(id+"F2.wireOp",EDGE,"E11.3.0.0");Q22=makeQuery(id+"F2.imprint","IMPRINT",FACE,{"disambiguationData":[TD([[makeQuery(id+"F2.imprint","IMPRINT",EDGE,{"derivedFrom":subQ1}),-1.0]])]});}
            var Q23;
            {var subQ4=sQuery(id+"F2.wireOp",EDGE,"E11.2.0.0");Q23=makeQuery(id+"F2.imprint","IMPRINT",FACE,{"disambiguationData":[TD([[makeQuery(id+"F2.imprint","IMPRINT",EDGE,{"derivedFrom":subQ4}),-1.0]])]});}
            var Q24;
            {var subQ1=sQuery(id+"F2.wireOp",EDGE,"E11.2.0.3");Q24=makeQuery(id+"F2.imprint","IMPRINT",FACE,{"disambiguationData":[TD([[makeQuery(id+"F2.imprint","IMPRINT",EDGE,{"derivedFrom":subQ1}),-1.0]])]});}
            var Q25;
            {var subQ1=sQuery(id+"F2.wireOp",EDGE,"E11.1.0.3");Q25=makeQuery(id+"F2.imprint","IMPRINT",FACE,{"disambiguationData":[TD([[makeQuery(id+"F2.imprint","IMPRINT",EDGE,{"derivedFrom":subQ1}),-1.0]])]});}
            var Q26;
            {var subQ4=sQuery(id+"F2.wireOp",EDGE,"E11.1.0.0");Q26=makeQuery(id+"F2.imprint","IMPRINT",FACE,{"disambiguationData":[TD([[makeQuery(id+"F2.imprint","IMPRINT",EDGE,{"derivedFrom":subQ4}),-1.0]])]});}
            var Q27;
            {var subQ0=sQuery(id+"F2.wireOp",EDGE,"E10.4");Q27=makeQuery(id+"F2.imprint","IMPRINT",FACE,{"disambiguationData":[TD([[makeQuery(id+"F2.imprint","IMPRINT",EDGE,{"derivedFrom":subQ0}),-1.0]])]});}
            var Q28;
            {var subQ1=sQuery(id+"F2.wireOp",EDGE,"E10.1");Q28=makeQuery(id+"F2.imprint","IMPRINT",FACE,{"disambiguationData":[TD([[makeQuery(id+"F2.imprint","IMPRINT",EDGE,{"derivedFrom":subQ1}),-1.0]])]});}
            var Q29;
            Q29=makeQuery(id+"F2.imprint","IMPRINT",FACE,{"disambiguationData":[TD([[makeQuery(id+"F2.imprint","IMPRINT",EDGE,{"derivedFrom":sQuery(id+"F2.wireOp",EDGE,"E11.0.1.0")}),-1.0]])]});
            var Q30;
            Q30=makeQuery(id+"F2.imprint","IMPRINT",FACE,{"disambiguationData":[TD([[makeQuery(id+"F2.imprint","IMPRINT",EDGE,{"derivedFrom":sQuery(id+"F2.wireOp",EDGE,"E11.0.2.0")}),-1.0]])]});
            var Q31;
            Q31=makeQuery(id+"F2.imprint","IMPRINT",FACE,{"disambiguationData":[TD([[makeQuery(id+"F2.imprint","IMPRINT",EDGE,{"derivedFrom":sQuery(id+"F2.wireOp",EDGE,"E11.1.2.0")}),-1.0]])]});
            var Q32;
            Q32=makeQuery(id+"F2.imprint","IMPRINT",FACE,{"disambiguationData":[TD([[makeQuery(id+"F2.imprint","IMPRINT",EDGE,{"derivedFrom":sQuery(id+"F2.wireOp",EDGE,"E11.1.1.0")}),-1.0]])]});
            var Q33;
            Q33=makeQuery(id+"F2.imprint","IMPRINT",FACE,{"disambiguationData":[TD([[makeQuery(id+"F2.imprint","IMPRINT",EDGE,{"derivedFrom":sQuery(id+"F2.wireOp",EDGE,"E11.1.3.0")}),-1.0]])]});
            var Q34;
            Q34=makeQuery(id+"F2.imprint","IMPRINT",FACE,{"disambiguationData":[TD([[makeQuery(id+"F2.imprint","IMPRINT",EDGE,{"derivedFrom":sQuery(id+"F2.wireOp",EDGE,"E11.0.3.0")}),-1.0]])]});
            var Q35;
            Q35=makeQuery(id+"F2.imprint","IMPRINT",FACE,{"disambiguationData":[TD([[makeQuery(id+"F2.imprint","IMPRINT",EDGE,{"derivedFrom":sQuery(id+"F2.wireOp",EDGE,"E11.0.4.0")}),-1.0]])]});
            var Q36;
            Q36=makeQuery(id+"F2.imprint","IMPRINT",FACE,{"disambiguationData":[TD([[makeQuery(id+"F2.imprint","IMPRINT",EDGE,{"derivedFrom":sQuery(id+"F2.wireOp",EDGE,"E11.1.4.0")}),-1.0]])]});
            var Q37;
            Q37=makeQuery(id+"F2.imprint","IMPRINT",FACE,{"disambiguationData":[TD([[makeQuery(id+"F2.imprint","IMPRINT",EDGE,{"derivedFrom":sQuery(id+"F2.wireOp",EDGE,"E11.1.5.0")}),-1.0]])]});
            var Q38;
            Q38=makeQuery(id+"F2.imprint","IMPRINT",FACE,{"disambiguationData":[TD([[makeQuery(id+"F2.imprint","IMPRINT",EDGE,{"derivedFrom":sQuery(id+"F2.wireOp",EDGE,"E11.1.6.0")}),-1.0]])]});
            var Q39;
            Q39=makeQuery(id+"F2.imprint","IMPRINT",FACE,{"disambiguationData":[TD([[makeQuery(id+"F2.imprint","IMPRINT",EDGE,{"derivedFrom":sQuery(id+"F2.wireOp",EDGE,"E11.1.7.0")}),-1.0]])]});
            var Q40;
            Q40=makeQuery(id+"F2.imprint","IMPRINT",FACE,{"disambiguationData":[TD([[makeQuery(id+"F2.imprint","IMPRINT",EDGE,{"derivedFrom":sQuery(id+"F2.wireOp",EDGE,"E11.1.8.0")}),-1.0]])]});
            var Q41;
            Q41=makeQuery(id+"F2.imprint","IMPRINT",FACE,{"disambiguationData":[TD([[makeQuery(id+"F2.imprint","IMPRINT",EDGE,{"derivedFrom":sQuery(id+"F2.wireOp",EDGE,"E11.1.9.0")}),-1.0]])]});
            var Q42;
            Q42=makeQuery(id+"F2.imprint","IMPRINT",FACE,{"disambiguationData":[TD([[makeQuery(id+"F2.imprint","IMPRINT",EDGE,{"derivedFrom":sQuery(id+"F2.wireOp",EDGE,"E11.0.9.0")}),-1.0]])]});
            var Q43;
            Q43=makeQuery(id+"F2.imprint","IMPRINT",FACE,{"disambiguationData":[TD([[makeQuery(id+"F2.imprint","IMPRINT",EDGE,{"derivedFrom":sQuery(id+"F2.wireOp",EDGE,"E11.0.8.0")}),-1.0]])]});
            var Q44;
            Q44=makeQuery(id+"F2.imprint","IMPRINT",FACE,{"disambiguationData":[TD([[makeQuery(id+"F2.imprint","IMPRINT",EDGE,{"derivedFrom":sQuery(id+"F2.wireOp",EDGE,"E11.0.7.0")}),-1.0]])]});
            var Q45;
            Q45=makeQuery(id+"F2.imprint","IMPRINT",FACE,{"disambiguationData":[TD([[makeQuery(id+"F2.imprint","IMPRINT",EDGE,{"derivedFrom":sQuery(id+"F2.wireOp",EDGE,"E11.0.6.0")}),-1.0]])]});
            var Q46;
            Q46=makeQuery(id+"F2.imprint","IMPRINT",FACE,{"disambiguationData":[TD([[makeQuery(id+"F2.imprint","IMPRINT",EDGE,{"derivedFrom":sQuery(id+"F2.wireOp",EDGE,"E11.0.5.0")}),-1.0]])]});
            var Q47;
            Q47=makeQuery(id+"F2.imprint","IMPRINT",FACE,{"disambiguationData":[TD([[makeQuery(id+"F2.imprint","IMPRINT",EDGE,{"derivedFrom":sQuery(id+"F2.wireOp",EDGE,"E11.2.1.0")}),-1.0]])]});
            var Q48;
            Q48=makeQuery(id+"F2.imprint","IMPRINT",FACE,{"disambiguationData":[TD([[makeQuery(id+"F2.imprint","IMPRINT",EDGE,{"derivedFrom":sQuery(id+"F2.wireOp",EDGE,"E11.2.2.0")}),-1.0]])]});
            var Q49;
            Q49=makeQuery(id+"F2.imprint","IMPRINT",FACE,{"disambiguationData":[TD([[makeQuery(id+"F2.imprint","IMPRINT",EDGE,{"derivedFrom":sQuery(id+"F2.wireOp",EDGE,"E11.3.2.0")}),-1.0]])]});
            var Q50;
            Q50=makeQuery(id+"F2.imprint","IMPRINT",FACE,{"disambiguationData":[TD([[makeQuery(id+"F2.imprint","IMPRINT",EDGE,{"derivedFrom":sQuery(id+"F2.wireOp",EDGE,"E11.3.1.0")}),-1.0]])]});
            var Q51;
            Q51=makeQuery(id+"F2.imprint","IMPRINT",FACE,{"disambiguationData":[TD([[makeQuery(id+"F2.imprint","IMPRINT",EDGE,{"derivedFrom":sQuery(id+"F2.wireOp",EDGE,"E11.3.3.0")}),-1.0]])]});
            var Q52;
            Q52=makeQuery(id+"F2.imprint","IMPRINT",FACE,{"disambiguationData":[TD([[makeQuery(id+"F2.imprint","IMPRINT",EDGE,{"derivedFrom":sQuery(id+"F2.wireOp",EDGE,"E11.2.3.0")}),-1.0]])]});
            var Q53;
            Q53=makeQuery(id+"F2.imprint","IMPRINT",FACE,{"disambiguationData":[TD([[makeQuery(id+"F2.imprint","IMPRINT",EDGE,{"derivedFrom":sQuery(id+"F2.wireOp",EDGE,"E11.2.4.0")}),-1.0]])]});
            var Q54;
            Q54=makeQuery(id+"F2.imprint","IMPRINT",FACE,{"disambiguationData":[TD([[makeQuery(id+"F2.imprint","IMPRINT",EDGE,{"derivedFrom":sQuery(id+"F2.wireOp",EDGE,"E11.2.5.0")}),-1.0]])]});
            var Q55;
            Q55=makeQuery(id+"F2.imprint","IMPRINT",FACE,{"disambiguationData":[TD([[makeQuery(id+"F2.imprint","IMPRINT",EDGE,{"derivedFrom":sQuery(id+"F2.wireOp",EDGE,"E11.2.6.0")}),-1.0]])]});
            var Q56;
            Q56=makeQuery(id+"F2.imprint","IMPRINT",FACE,{"disambiguationData":[TD([[makeQuery(id+"F2.imprint","IMPRINT",EDGE,{"derivedFrom":sQuery(id+"F2.wireOp",EDGE,"E11.3.6.0")}),-1.0]])]});
            var Q57;
            Q57=makeQuery(id+"F2.imprint","IMPRINT",FACE,{"disambiguationData":[TD([[makeQuery(id+"F2.imprint","IMPRINT",EDGE,{"derivedFrom":sQuery(id+"F2.wireOp",EDGE,"E11.3.5.0")}),-1.0]])]});
            var Q58;
            Q58=makeQuery(id+"F2.imprint","IMPRINT",FACE,{"disambiguationData":[TD([[makeQuery(id+"F2.imprint","IMPRINT",EDGE,{"derivedFrom":sQuery(id+"F2.wireOp",EDGE,"E11.3.4.0")}),-1.0]])]});
            var Q59;
            Q59=makeQuery(id+"F2.imprint","IMPRINT",FACE,{"disambiguationData":[TD([[makeQuery(id+"F2.imprint","IMPRINT",EDGE,{"derivedFrom":sQuery(id+"F2.wireOp",EDGE,"E11.3.7.0")}),-1.0]])]});
            var Q60;
            Q60=makeQuery(id+"F2.imprint","IMPRINT",FACE,{"disambiguationData":[TD([[makeQuery(id+"F2.imprint","IMPRINT",EDGE,{"derivedFrom":sQuery(id+"F2.wireOp",EDGE,"E11.2.7.0")}),-1.0]])]});
            var Q61;
            Q61=makeQuery(id+"F2.imprint","IMPRINT",FACE,{"disambiguationData":[TD([[makeQuery(id+"F2.imprint","IMPRINT",EDGE,{"derivedFrom":sQuery(id+"F2.wireOp",EDGE,"E11.2.8.0")}),-1.0]])]});
            var Q62;
            Q62=makeQuery(id+"F2.imprint","IMPRINT",FACE,{"disambiguationData":[TD([[makeQuery(id+"F2.imprint","IMPRINT",EDGE,{"derivedFrom":sQuery(id+"F2.wireOp",EDGE,"E11.2.9.0")}),-1.0]])]});
            var Q63;
            Q63=makeQuery(id+"F2.imprint","IMPRINT",FACE,{"disambiguationData":[TD([[makeQuery(id+"F2.imprint","IMPRINT",EDGE,{"derivedFrom":sQuery(id+"F2.wireOp",EDGE,"E11.3.9.0")}),-1.0]])]});
            var Q64;
            Q64=makeQuery(id+"F2.imprint","IMPRINT",FACE,{"disambiguationData":[TD([[makeQuery(id+"F2.imprint","IMPRINT",EDGE,{"derivedFrom":sQuery(id+"F2.wireOp",EDGE,"E11.3.8.0")}),-1.0]])]});
            var Q65;
            Q65=makeQuery(id+"F2.imprint","IMPRINT",FACE,{"disambiguationData":[TD([[makeQuery(id+"F2.imprint","IMPRINT",EDGE,{"derivedFrom":sQuery(id+"F2.wireOp",EDGE,"E11.6.1.0")}),-1.0]])]});
            var Q66;
            Q66=makeQuery(id+"F2.imprint","IMPRINT",FACE,{"disambiguationData":[TD([[makeQuery(id+"F2.imprint","IMPRINT",EDGE,{"derivedFrom":sQuery(id+"F2.wireOp",EDGE,"E11.5.2.0")}),-1.0]])]});
            var Q67;
            Q67=makeQuery(id+"F2.imprint","IMPRINT",FACE,{"disambiguationData":[TD([[makeQuery(id+"F2.imprint","IMPRINT",EDGE,{"derivedFrom":sQuery(id+"F2.wireOp",EDGE,"E11.4.3.0")}),-1.0]])]});
            var Q68;
            Q68=makeQuery(id+"F2.imprint","IMPRINT",FACE,{"disambiguationData":[TD([[makeQuery(id+"F2.imprint","IMPRINT",EDGE,{"derivedFrom":sQuery(id+"F2.wireOp",EDGE,"E11.4.2.0")}),-1.0]])]});
            var Q69;
            Q69=makeQuery(id+"F2.imprint","IMPRINT",FACE,{"disambiguationData":[TD([[makeQuery(id+"F2.imprint","IMPRINT",EDGE,{"derivedFrom":sQuery(id+"F2.wireOp",EDGE,"E11.4.1.0")}),-1.0]])]});
            var Q70;
            Q70=makeQuery(id+"F2.imprint","IMPRINT",FACE,{"disambiguationData":[TD([[makeQuery(id+"F2.imprint","IMPRINT",EDGE,{"derivedFrom":sQuery(id+"F2.wireOp",EDGE,"E11.5.1.0")}),-1.0]])]});
            var Q71;
            Q71=makeQuery(id+"F2.imprint","IMPRINT",FACE,{"disambiguationData":[TD([[makeQuery(id+"F2.imprint","IMPRINT",EDGE,{"derivedFrom":sQuery(id+"F2.wireOp",EDGE,"E11.7.1.0")}),-1.0]])]});
            var Q72;
            Q72=makeQuery(id+"F2.imprint","IMPRINT",FACE,{"disambiguationData":[TD([[makeQuery(id+"F2.imprint","IMPRINT",EDGE,{"derivedFrom":sQuery(id+"F2.wireOp",EDGE,"E11.6.2.0")}),-1.0]])]});
            var Q73;
            Q73=makeQuery(id+"F2.imprint","IMPRINT",FACE,{"disambiguationData":[TD([[makeQuery(id+"F2.imprint","IMPRINT",EDGE,{"derivedFrom":sQuery(id+"F2.wireOp",EDGE,"E11.5.3.0")}),-1.0]])]});
            var Q74;
            Q74=makeQuery(id+"F2.imprint","IMPRINT",FACE,{"disambiguationData":[TD([[makeQuery(id+"F2.imprint","IMPRINT",EDGE,{"derivedFrom":sQuery(id+"F2.wireOp",EDGE,"E11.4.4.0")}),-1.0]])]});
            var Q75;
            Q75=makeQuery(id+"F2.imprint","IMPRINT",FACE,{"disambiguationData":[TD([[makeQuery(id+"F2.imprint","IMPRINT",EDGE,{"derivedFrom":sQuery(id+"F2.wireOp",EDGE,"E11.4.5.0")}),-1.0]])]});
            var Q76;
            Q76=makeQuery(id+"F2.imprint","IMPRINT",FACE,{"disambiguationData":[TD([[makeQuery(id+"F2.imprint","IMPRINT",EDGE,{"derivedFrom":sQuery(id+"F2.wireOp",EDGE,"E11.5.4.0")}),-1.0]])]});
            var Q77;
            Q77=makeQuery(id+"F2.imprint","IMPRINT",FACE,{"disambiguationData":[TD([[makeQuery(id+"F2.imprint","IMPRINT",EDGE,{"derivedFrom":sQuery(id+"F2.wireOp",EDGE,"E11.5.5.0")}),-1.0]])]});
            var Q78;
            Q78=makeQuery(id+"F2.imprint","IMPRINT",FACE,{"disambiguationData":[TD([[makeQuery(id+"F2.imprint","IMPRINT",EDGE,{"derivedFrom":sQuery(id+"F2.wireOp",EDGE,"E11.5.6.0")}),-1.0]])]});
            var Q79;
            Q79=makeQuery(id+"F2.imprint","IMPRINT",FACE,{"disambiguationData":[TD([[makeQuery(id+"F2.imprint","IMPRINT",EDGE,{"derivedFrom":sQuery(id+"F2.wireOp",EDGE,"E11.4.6.0")}),-1.0]])]});
            var Q80;
            Q80=makeQuery(id+"F2.imprint","IMPRINT",FACE,{"disambiguationData":[TD([[makeQuery(id+"F2.imprint","IMPRINT",EDGE,{"derivedFrom":sQuery(id+"F2.wireOp",EDGE,"E11.4.7.0")}),-1.0]])]});
            var Q81;
            Q81=makeQuery(id+"F2.imprint","IMPRINT",FACE,{"disambiguationData":[TD([[makeQuery(id+"F2.imprint","IMPRINT",EDGE,{"derivedFrom":sQuery(id+"F2.wireOp",EDGE,"E11.4.8.0")}),-1.0]])]});
            var Q82;
            Q82=makeQuery(id+"F2.imprint","IMPRINT",FACE,{"disambiguationData":[TD([[makeQuery(id+"F2.imprint","IMPRINT",EDGE,{"derivedFrom":sQuery(id+"F2.wireOp",EDGE,"E11.4.9.0")}),-1.0]])]});
            var Q83;
            Q83=makeQuery(id+"F2.imprint","IMPRINT",FACE,{"disambiguationData":[TD([[makeQuery(id+"F2.imprint","IMPRINT",EDGE,{"derivedFrom":sQuery(id+"F2.wireOp",EDGE,"E11.5.9.0")}),-1.0]])]});
            var Q84;
            Q84=makeQuery(id+"F2.imprint","IMPRINT",FACE,{"disambiguationData":[TD([[makeQuery(id+"F2.imprint","IMPRINT",EDGE,{"derivedFrom":sQuery(id+"F2.wireOp",EDGE,"E11.5.8.0")}),-1.0]])]});
            var Q85;
            Q85=makeQuery(id+"F2.imprint","IMPRINT",FACE,{"disambiguationData":[TD([[makeQuery(id+"F2.imprint","IMPRINT",EDGE,{"derivedFrom":sQuery(id+"F2.wireOp",EDGE,"E11.5.7.0")}),-1.0]])]});
            var Q86;
            Q86=makeQuery(id+"F2.imprint","IMPRINT",FACE,{"disambiguationData":[TD([[makeQuery(id+"F2.imprint","IMPRINT",EDGE,{"derivedFrom":sQuery(id+"F2.wireOp",EDGE,"E11.8.1.0")}),-1.0]])]});
            var Q87;
            Q87=makeQuery(id+"F2.imprint","IMPRINT",FACE,{"disambiguationData":[TD([[makeQuery(id+"F2.imprint","IMPRINT",EDGE,{"derivedFrom":sQuery(id+"F2.wireOp",EDGE,"E11.7.2.0")}),-1.0]])]});
            var Q88;
            Q88=makeQuery(id+"F2.imprint","IMPRINT",FACE,{"disambiguationData":[TD([[makeQuery(id+"F2.imprint","IMPRINT",EDGE,{"derivedFrom":sQuery(id+"F2.wireOp",EDGE,"E11.6.3.0")}),-1.0]])]});
            var Q89;
            Q89=makeQuery(id+"F2.imprint","IMPRINT",FACE,{"disambiguationData":[TD([[makeQuery(id+"F2.imprint","IMPRINT",EDGE,{"derivedFrom":sQuery(id+"F2.wireOp",EDGE,"E11.8.2.0")}),-1.0]])]});
            var Q90;
            Q90=makeQuery(id+"F2.imprint","IMPRINT",FACE,{"disambiguationData":[TD([[makeQuery(id+"F2.imprint","IMPRINT",EDGE,{"derivedFrom":sQuery(id+"F2.wireOp",EDGE,"E11.7.3.0")}),-1.0]])]});
            var Q91;
            Q91=makeQuery(id+"F2.imprint","IMPRINT",FACE,{"disambiguationData":[TD([[makeQuery(id+"F2.imprint","IMPRINT",EDGE,{"derivedFrom":sQuery(id+"F2.wireOp",EDGE,"E11.6.4.0")}),-1.0]])]});
            var Q92;
            Q92=makeQuery(id+"F2.imprint","IMPRINT",FACE,{"disambiguationData":[TD([[makeQuery(id+"F2.imprint","IMPRINT",EDGE,{"derivedFrom":sQuery(id+"F2.wireOp",EDGE,"E11.8.3.0")}),-1.0]])]});
            var Q93;
            Q93=makeQuery(id+"F2.imprint","IMPRINT",FACE,{"disambiguationData":[TD([[makeQuery(id+"F2.imprint","IMPRINT",EDGE,{"derivedFrom":sQuery(id+"F2.wireOp",EDGE,"E11.7.4.0")}),-1.0]])]});
            var Q94;
            Q94=makeQuery(id+"F2.imprint","IMPRINT",FACE,{"disambiguationData":[TD([[makeQuery(id+"F2.imprint","IMPRINT",EDGE,{"derivedFrom":sQuery(id+"F2.wireOp",EDGE,"E11.6.5.0")}),-1.0]])]});
            var Q95;
            Q95=makeQuery(id+"F2.imprint","IMPRINT",FACE,{"disambiguationData":[TD([[makeQuery(id+"F2.imprint","IMPRINT",EDGE,{"derivedFrom":sQuery(id+"F2.wireOp",EDGE,"E11.8.4.0")}),-1.0]])]});
            var Q96;
            Q96=makeQuery(id+"F2.imprint","IMPRINT",FACE,{"disambiguationData":[TD([[makeQuery(id+"F2.imprint","IMPRINT",EDGE,{"derivedFrom":sQuery(id+"F2.wireOp",EDGE,"E11.7.5.0")}),-1.0]])]});
            var Q97;
            Q97=makeQuery(id+"F2.imprint","IMPRINT",FACE,{"disambiguationData":[TD([[makeQuery(id+"F2.imprint","IMPRINT",EDGE,{"derivedFrom":sQuery(id+"F2.wireOp",EDGE,"E11.6.6.0")}),-1.0]])]});
            var Q98;
            Q98=makeQuery(id+"F2.imprint","IMPRINT",FACE,{"disambiguationData":[TD([[makeQuery(id+"F2.imprint","IMPRINT",EDGE,{"derivedFrom":sQuery(id+"F2.wireOp",EDGE,"E11.6.7.0")}),-1.0]])]});
            var Q99;
            Q99=makeQuery(id+"F2.imprint","IMPRINT",FACE,{"disambiguationData":[TD([[makeQuery(id+"F2.imprint","IMPRINT",EDGE,{"derivedFrom":sQuery(id+"F2.wireOp",EDGE,"E11.7.6.0")}),-1.0]])]});
            var Q100;
            Q100=makeQuery(id+"F2.imprint","IMPRINT",FACE,{"disambiguationData":[TD([[makeQuery(id+"F2.imprint","IMPRINT",EDGE,{"derivedFrom":sQuery(id+"F2.wireOp",EDGE,"E11.8.5.0")}),-1.0]])]});
            var Q101;
            Q101=makeQuery(id+"F2.imprint","IMPRINT",FACE,{"disambiguationData":[TD([[makeQuery(id+"F2.imprint","IMPRINT",EDGE,{"derivedFrom":sQuery(id+"F2.wireOp",EDGE,"E11.8.6.0")}),-1.0]])]});
            var Q102;
            Q102=makeQuery(id+"F2.imprint","IMPRINT",FACE,{"disambiguationData":[TD([[makeQuery(id+"F2.imprint","IMPRINT",EDGE,{"derivedFrom":sQuery(id+"F2.wireOp",EDGE,"E11.8.7.0")}),-1.0]])]});
            var Q103;
            Q103=makeQuery(id+"F2.imprint","IMPRINT",FACE,{"disambiguationData":[TD([[makeQuery(id+"F2.imprint","IMPRINT",EDGE,{"derivedFrom":sQuery(id+"F2.wireOp",EDGE,"E11.7.7.0")}),-1.0]])]});
            var Q104;
            Q104=makeQuery(id+"F2.imprint","IMPRINT",FACE,{"disambiguationData":[TD([[makeQuery(id+"F2.imprint","IMPRINT",EDGE,{"derivedFrom":sQuery(id+"F2.wireOp",EDGE,"E11.7.8.0")}),-1.0]])]});
            var Q105;
            Q105=makeQuery(id+"F2.imprint","IMPRINT",FACE,{"disambiguationData":[TD([[makeQuery(id+"F2.imprint","IMPRINT",EDGE,{"derivedFrom":sQuery(id+"F2.wireOp",EDGE,"E11.6.8.0")}),-1.0]])]});
            var Q106;
            Q106=makeQuery(id+"F2.imprint","IMPRINT",FACE,{"disambiguationData":[TD([[makeQuery(id+"F2.imprint","IMPRINT",EDGE,{"derivedFrom":sQuery(id+"F2.wireOp",EDGE,"E11.6.9.0")}),-1.0]])]});
            var Q107;
            Q107=makeQuery(id+"F2.imprint","IMPRINT",FACE,{"disambiguationData":[TD([[makeQuery(id+"F2.imprint","IMPRINT",EDGE,{"derivedFrom":sQuery(id+"F2.wireOp",EDGE,"E11.7.9.0")}),-1.0]])]});
            var Q108;
            Q108=makeQuery(id+"F2.imprint","IMPRINT",FACE,{"disambiguationData":[TD([[makeQuery(id+"F2.imprint","IMPRINT",EDGE,{"derivedFrom":sQuery(id+"F2.wireOp",EDGE,"E11.8.8.0")}),-1.0]])]});
            var Q109;
            Q109=makeQuery(id+"F2.imprint","IMPRINT",FACE,{"disambiguationData":[TD([[makeQuery(id+"F2.imprint","IMPRINT",EDGE,{"derivedFrom":sQuery(id+"F2.wireOp",EDGE,"E11.8.9.0")}),-1.0]])]});
            extrude(context, id + "F6", {"entities" : qUnion([Q0, Q1, Q2, Q3, Q4, Q5, Q6, Q7, Q8, Q9, Q10, Q11, Q12, Q13, Q14, Q15, Q16, Q17, Q18, Q19, Q20, Q21, Q22, Q23, Q24, Q25, Q26, Q27, Q28, Q29, Q30, Q31, Q32, Q33, Q34, Q35, Q36, Q37, Q38, Q39, Q40, Q41, Q42, Q43, Q44, Q45, Q46, Q47, Q48, Q49, Q50, Q51, Q52, Q53, Q54, Q55, Q56, Q57, Q58, Q59, Q60, Q61, Q62, Q63, Q64, Q65, Q66, Q67, Q68, Q69, Q70, Q71, Q72, Q73, Q74, Q75, Q76, Q77, Q78, Q79, Q80, Q81, Q82, Q83, Q84, Q85, Q86, Q87, Q88, Q89, Q90, Q91, Q92, Q93, Q94, Q95, Q96, Q97, Q98, Q99, Q100, Q101, Q102, Q103, Q104, Q105, Q106, Q107, Q108, Q109]), "operationType" : NewBodyOperationType.REMOVE, "endBound" : BoundingType.THROUGH_ALL, "oppositeDirection" : true, "depth" : 25 * mm, "offsetDistance" : 25 * mm});
        }
        {
            var Q0;
            Q0=makeQuery(id+"F1.opExtrude","CAP_FACE",FACE,{"disambiguationData":[OSD([sQuery(id+"F0.wireOp",EDGE,"E0.bottom"),sQuery(id+"F0.wireOp",EDGE,"E0.top"),sQuery(id+"F0.wireOp",EDGE,"E0.left"),sQuery(id+"F0.wireOp",EDGE,"E0.right")])],"isStart":true});
            var sketch = newSketch(context, id + "F7", { "sketchPlane" : qUnion([Q0])});
            skCircle(sketch, "E25", {"center": v(0, 0) * mm, "radius": 46 * mm});
            skLineSegment(sketch, "E26", {"start": v(-27.6, 36.8) * mm, "end": v(27.6, 36.8) * mm});
            skLineSegment(sketch, "E27.MirrorCS", {"start": v(-27.6, -36.8) * mm, "end": v(27.6, -36.8) * mm});
            skLineSegment(sketch, "E28", {"start": v(-36.8, 27.6) * mm, "end": v(36.8, 27.6) * mm});
            skLineSegment(sketch, "E29", {"start": v(-42.16, 18.4) * mm, "end": v(42.16, 18.4) * mm});
            skLineSegment(sketch, "E30", {"start": v(-45.07, 9.2) * mm, "end": v(45.07, 9.2) * mm});
            skLineSegment(sketch, "E31.MirrorCS", {"start": v(-45.07, -9.2) * mm, "end": v(45.07, -9.2) * mm});
            skLineSegment(sketch, "E32.MirrorCS", {"start": v(-42.16, -18.4) * mm, "end": v(42.16, -18.4) * mm});
            skLineSegment(sketch, "E33.MirrorCS", {"start": v(-36.8, -27.6) * mm, "end": v(36.8, -27.6) * mm});
            skLineSegment(sketch, "E34", {"start": v(-25.48, -38.3) * mm, "end": v(25.48, -38.3) * mm});
            skLineSegment(sketch, "E35", {"start": v(-35.63, -29.1) * mm, "end": v(35.63, -29.1) * mm});
            skLineSegment(sketch, "E36", {"start": v(-41.47, -19.9) * mm, "end": v(41.47, -19.9) * mm});
            skLineSegment(sketch, "E37", {"start": v(-44.74, -10.7) * mm, "end": v(44.74, -10.7) * mm});
            skLineSegment(sketch, "E38.MirrorCS", {"start": v(-25.48, 38.3) * mm, "end": v(25.48, 38.3) * mm});
            skLineSegment(sketch, "E39.MirrorCS", {"start": v(-35.63, 29.1) * mm, "end": v(35.63, 29.1) * mm});
            skLineSegment(sketch, "E40.MirrorCS", {"start": v(-41.47, 19.9) * mm, "end": v(41.47, 19.9) * mm});
            skLineSegment(sketch, "E41.MirrorCS", {"start": v(-44.74, 10.7) * mm, "end": v(44.74, 10.7) * mm});
            skLineSegment(sketch, "E42", {"start": v(-46, -0.75) * mm, "end": v(46, -0.75) * mm});
            skLineSegment(sketch, "E43", {"start": v(-46, 0.75) * mm, "end": v(46, 0.75) * mm});
            skSolve(sketch);
        }
        {
            var Q0;
            {var subQ0=sQuery(id+"F7.wireOp",EDGE,"E34");Q0=makeQuery(id+"F7.imprint","IMPRINT",FACE,{"disambiguationData":[TD([[makeQuery(id+"F7.imprint","IMPRINT",EDGE,{"derivedFrom":subQ0}),-1.0]])]});}
            var Q1;
            {var subQ0=sQuery(id+"F7.wireOp",EDGE,"E27.MirrorCS");Q1=makeQuery(id+"F7.imprint","IMPRINT",FACE,{"disambiguationData":[TD([[makeQuery(id+"F7.imprint","IMPRINT",EDGE,{"derivedFrom":subQ0}),1.0]])]});}
            var Q2;
            {var subQ0=sQuery(id+"F7.wireOp",EDGE,"E33.MirrorCS");Q2=makeQuery(id+"F7.imprint","IMPRINT",FACE,{"disambiguationData":[TD([[makeQuery(id+"F7.imprint","IMPRINT",EDGE,{"derivedFrom":subQ0}),1.0]])]});}
            var Q3;
            {var subQ0=sQuery(id+"F7.wireOp",EDGE,"E32.MirrorCS");Q3=makeQuery(id+"F7.imprint","IMPRINT",FACE,{"disambiguationData":[TD([[makeQuery(id+"F7.imprint","IMPRINT",EDGE,{"derivedFrom":subQ0}),1.0]])]});}
            var Q4;
            {var subQ0=sQuery(id+"F7.wireOp",EDGE,"E31.MirrorCS");Q4=makeQuery(id+"F7.imprint","IMPRINT",FACE,{"disambiguationData":[TD([[makeQuery(id+"F7.imprint","IMPRINT",EDGE,{"derivedFrom":subQ0}),1.0]])]});}
            var Q5;
            {var subQ0=sQuery(id+"F7.wireOp",EDGE,"E30");Q5=makeQuery(id+"F7.imprint","IMPRINT",FACE,{"disambiguationData":[TD([[makeQuery(id+"F7.imprint","IMPRINT",EDGE,{"derivedFrom":subQ0}),-1.0]])]});}
            var Q6;
            {var subQ0=sQuery(id+"F7.wireOp",EDGE,"E29");Q6=makeQuery(id+"F7.imprint","IMPRINT",FACE,{"disambiguationData":[TD([[makeQuery(id+"F7.imprint","IMPRINT",EDGE,{"derivedFrom":subQ0}),-1.0]])]});}
            var Q7;
            {var subQ0=sQuery(id+"F7.wireOp",EDGE,"E28");Q7=makeQuery(id+"F7.imprint","IMPRINT",FACE,{"disambiguationData":[TD([[makeQuery(id+"F7.imprint","IMPRINT",EDGE,{"derivedFrom":subQ0}),-1.0]])]});}
            var Q8;
            {var subQ0=sQuery(id+"F7.wireOp",EDGE,"E26");Q8=makeQuery(id+"F7.imprint","IMPRINT",FACE,{"disambiguationData":[TD([[makeQuery(id+"F7.imprint","IMPRINT",EDGE,{"derivedFrom":subQ0}),-1.0]])]});}
            var Q9;
            {var subQ0=sQuery(id+"F7.wireOp",EDGE,"E38.MirrorCS");Q9=makeQuery(id+"F7.imprint","IMPRINT",FACE,{"disambiguationData":[TD([[makeQuery(id+"F7.imprint","IMPRINT",EDGE,{"derivedFrom":subQ0}),1.0]])]});}
            extrude(context, id + "F8", {"entities" : qUnion([Q0, Q1, Q2, Q3, Q4, Q5, Q6, Q7, Q8, Q9]), "operationType" : NewBodyOperationType.REMOVE, "oppositeDirection" : true, "depth" : 25 * mm, "offsetDistance" : 25 * mm});
        }
        {
            var Q0;
            Q0=qCreatedBy(makeId("Top.planeOp"),FACE);
            var sketch = newSketch(context, id + "F9", { "sketchPlane" : qUnion([Q0])});
            skCircle(sketch, "E44", {"center": v(0, 0) * mm, "radius": 45.58 * mm});
            skSolve(sketch);
        }
        {
            var Q0;
            Q0=qSketchRegion(id+"F9",true);
            extrude(context, id + "F10", {"entities" : qUnion([Q0]), "operationType" : NewBodyOperationType.REMOVE, "depth" : 50.9 * mm, "offsetDistance" : 25 * mm, "hasSecondDirection" : true, "secondDirectionOppositeDirection" : false, "secondDirectionDepth" : 1.5 * mm});
        }
    });
